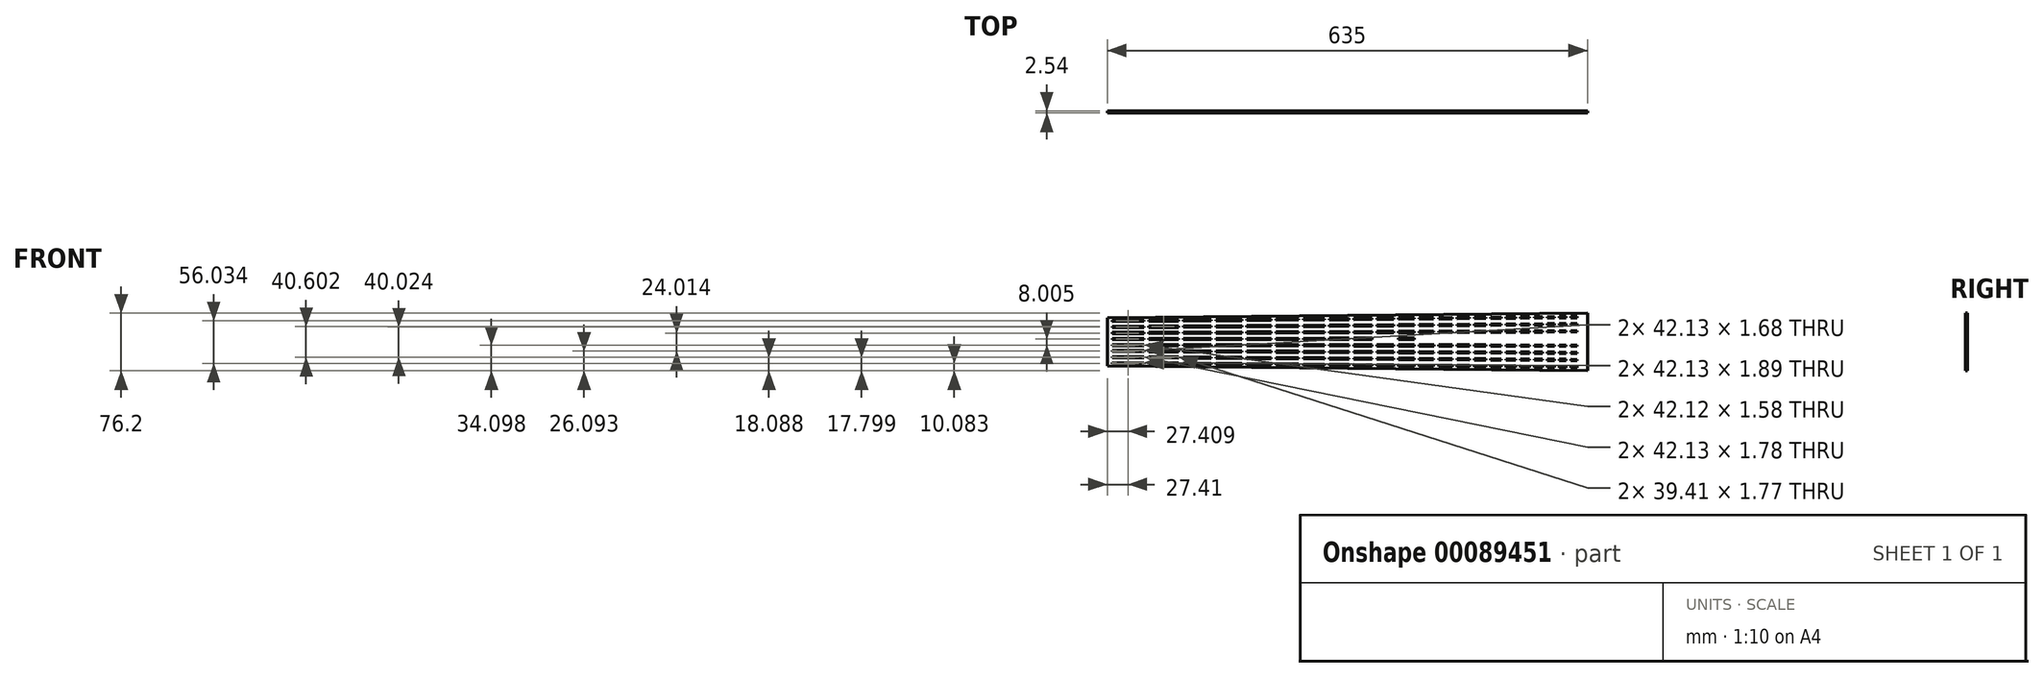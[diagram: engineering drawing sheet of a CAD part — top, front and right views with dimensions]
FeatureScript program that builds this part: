
annotation { "Feature Type Name" : "Feature", "Feature Type Description" : "" }
export const myFeature = defineFeature(function(context is Context, id is Id, definition is map)
    precondition{}
    {
        {
            var Q0;
            Q0=qCreatedBy(makeId("Front.planeOp"),FACE);
            var sketch = newSketch(context, id + "F0", { "sketchPlane" : qUnion([Q0])});
            skLineSegment(sketch, "E0", {"start": v(0, 3.97) * mm, "end": v(646.64, -1.59) * mm, "construction": true});
            skLineSegment(sketch, "E1", {"start": v(0, 4.73) * mm, "end": v(642.96, -0.8) * mm, "construction": true});
            skLineSegment(sketch, "E2", {"start": v(6.35, 3.91) * mm, "end": v(6.36, 4.68) * mm});
            skLineSegment(sketch, "E3", {"start": v(6.36, 4.68) * mm, "end": v(48.48, 4.31) * mm});
            skLineSegment(sketch, "E4", {"start": v(48.48, 4.31) * mm, "end": v(48.47, 3.55) * mm});
            skLineSegment(sketch, "E5", {"start": v(54.82, 3.5) * mm, "end": v(54.82, 4.26) * mm});
            skLineSegment(sketch, "E6", {"start": v(54.82, 4.26) * mm, "end": v(94.22, 3.92) * mm});
            skLineSegment(sketch, "E7", {"start": v(94.22, 3.92) * mm, "end": v(94.22, 3.16) * mm});
            skLineSegment(sketch, "E8", {"start": v(100.57, 3.1) * mm, "end": v(100.57, 3.87) * mm});
            skLineSegment(sketch, "E9", {"start": v(100.57, 3.87) * mm, "end": v(137.4, 3.55) * mm});
            skLineSegment(sketch, "E10", {"start": v(137.4, 3.55) * mm, "end": v(137.4, 2.79) * mm});
            skLineSegment(sketch, "E11", {"start": v(143.75, 2.73) * mm, "end": v(143.75, 3.5) * mm});
            skLineSegment(sketch, "E12", {"start": v(143.75, 3.5) * mm, "end": v(178.15, 3.2) * mm});
            skLineSegment(sketch, "E13", {"start": v(178.15, 3.2) * mm, "end": v(178.15, 2.44) * mm});
            skLineSegment(sketch, "E14", {"start": v(184.5, 2.38) * mm, "end": v(184.5, 3.15) * mm});
            skLineSegment(sketch, "E15", {"start": v(184.5, 3.15) * mm, "end": v(216.63, 2.87) * mm, "construction": true});
            skLineSegment(sketch, "E16", {"start": v(216.63, 2.87) * mm, "end": v(216.62, 2.1) * mm});
            skLineSegment(sketch, "E17", {"start": v(222.97, 2.05) * mm, "end": v(222.98, 2.81) * mm});
            skLineSegment(sketch, "E18", {"start": v(222.98, 2.81) * mm, "end": v(252.94, 2.56) * mm});
            skLineSegment(sketch, "E19", {"start": v(252.94, 2.56) * mm, "end": v(252.93, 1.8) * mm});
            skLineSegment(sketch, "E20", {"start": v(259.28, 1.74) * mm, "end": v(259.29, 2.5) * mm});
            skLineSegment(sketch, "E21", {"start": v(259.29, 2.5) * mm, "end": v(287.21, 2.26) * mm});
            skLineSegment(sketch, "E22", {"start": v(287.21, 2.26) * mm, "end": v(287.2, 1.5) * mm});
            skLineSegment(sketch, "E23", {"start": v(293.56, 1.45) * mm, "end": v(293.56, 2.2) * mm});
            skLineSegment(sketch, "E24", {"start": v(293.56, 2.2) * mm, "end": v(319.56, 1.98) * mm});
            skLineSegment(sketch, "E25", {"start": v(319.56, 1.98) * mm, "end": v(319.55, 1.22) * mm});
            skLineSegment(sketch, "E26", {"start": v(325.9, 1.17) * mm, "end": v(325.91, 1.93) * mm});
            skLineSegment(sketch, "E27", {"start": v(325.91, 1.93) * mm, "end": v(350.1, 1.72) * mm});
            skLineSegment(sketch, "E28", {"start": v(350.1, 1.72) * mm, "end": v(350.09, 0.96) * mm});
            skLineSegment(sketch, "E29", {"start": v(184.5, 3.15) * mm, "end": v(216.63, 2.87) * mm});
            skLineSegment(sketch, "E30", {"start": v(356.44, 0.9) * mm, "end": v(356.44, 1.67) * mm});
            skLineSegment(sketch, "E31", {"start": v(356.44, 1.67) * mm, "end": v(378.91, 1.47) * mm});
            skLineSegment(sketch, "E32", {"start": v(378.91, 1.47) * mm, "end": v(378.9, 0.71) * mm});
            skLineSegment(sketch, "E33", {"start": v(385.26, 0.66) * mm, "end": v(385.26, 1.42) * mm});
            skLineSegment(sketch, "E34", {"start": v(385.26, 1.42) * mm, "end": v(406.12, 1.24) * mm});
            skLineSegment(sketch, "E35", {"start": v(406.12, 1.24) * mm, "end": v(406.1, 0.48) * mm});
            skLineSegment(sketch, "E36", {"start": v(412.46, 0.42) * mm, "end": v(412.46, 1.19) * mm});
            skLineSegment(sketch, "E37", {"start": v(412.46, 1.19) * mm, "end": v(431.8, 1.02) * mm});
            skLineSegment(sketch, "E38", {"start": v(431.8, 1.02) * mm, "end": v(431.78, 0.26) * mm});
            skLineSegment(sketch, "E39", {"start": v(438.13, 0.2) * mm, "end": v(438.14, 0.97) * mm});
            skLineSegment(sketch, "E40", {"start": v(438.14, 0.97) * mm, "end": v(456.02, 0.81) * mm});
            skLineSegment(sketch, "E41", {"start": v(456.02, 0.81) * mm, "end": v(456.02, 0.05) * mm});
            skLineSegment(sketch, "E42", {"start": v(462.37, 0) * mm, "end": v(462.37, 0.76) * mm});
            skLineSegment(sketch, "E43", {"start": v(462.37, 0.76) * mm, "end": v(478.9, 0.62) * mm});
            skLineSegment(sketch, "E44", {"start": v(478.9, 0.62) * mm, "end": v(478.9, -0.15) * mm});
            skLineSegment(sketch, "E45", {"start": v(485.24, -0.2) * mm, "end": v(485.25, 0.56) * mm});
            skLineSegment(sketch, "E46", {"start": v(485.25, 0.56) * mm, "end": v(500.49, 0.43) * mm});
            skLineSegment(sketch, "E47", {"start": v(500.49, 0.43) * mm, "end": v(500.48, -0.33) * mm});
            skLineSegment(sketch, "E48", {"start": v(506.83, -0.39) * mm, "end": v(506.84, 0.38) * mm});
            skLineSegment(sketch, "E49", {"start": v(506.84, 0.38) * mm, "end": v(520.87, 0.26) * mm});
            skLineSegment(sketch, "E50", {"start": v(520.87, 0.26) * mm, "end": v(520.86, -0.5) * mm});
            skLineSegment(sketch, "E51", {"start": v(527.21, -0.56) * mm, "end": v(527.22, 0.2) * mm});
            skLineSegment(sketch, "E52", {"start": v(527.22, 0.2) * mm, "end": v(540.1, 0.09) * mm});
            skLineSegment(sketch, "E53", {"start": v(540.1, 0.09) * mm, "end": v(540.1, -0.67) * mm});
            skLineSegment(sketch, "E54", {"start": v(546.45, -0.73) * mm, "end": v(546.45, 0.04) * mm});
            skLineSegment(sketch, "E55", {"start": v(546.45, 0.04) * mm, "end": v(558.26, -0.07) * mm});
            skLineSegment(sketch, "E56", {"start": v(558.26, -0.07) * mm, "end": v(558.25, -0.83) * mm});
            skLineSegment(sketch, "E57", {"start": v(564.6, -0.88) * mm, "end": v(564.6, -0.12) * mm});
            skLineSegment(sketch, "E58", {"start": v(564.6, -0.12) * mm, "end": v(575.4, -0.21) * mm});
            skLineSegment(sketch, "E59", {"start": v(575.4, -0.21) * mm, "end": v(575.39, -0.98) * mm});
            skLineSegment(sketch, "E60", {"start": v(581.74, -1.03) * mm, "end": v(581.74, -0.27) * mm});
            skLineSegment(sketch, "E61", {"start": v(581.74, -0.27) * mm, "end": v(591.57, -0.35) * mm});
            skLineSegment(sketch, "E62", {"start": v(591.57, -0.35) * mm, "end": v(591.56, -1.11) * mm});
            skLineSegment(sketch, "E63", {"start": v(597.91, -1.17) * mm, "end": v(597.92, -0.4) * mm});
            skLineSegment(sketch, "E64", {"start": v(597.92, -0.4) * mm, "end": v(606.83, -0.48) * mm});
            skLineSegment(sketch, "E65", {"start": v(606.83, -0.48) * mm, "end": v(606.83, -1.25) * mm});
            skLineSegment(sketch, "E66", {"start": v(613.18, -1.3) * mm, "end": v(613.18, -0.54) * mm});
            skLineSegment(sketch, "E67", {"start": v(613.18, -0.54) * mm, "end": v(621.24, -0.6) * mm});
            skLineSegment(sketch, "E68", {"start": v(621.24, -0.6) * mm, "end": v(621.24, -1.37) * mm});
            skLineSegment(sketch, "E69.MirrorCS", {"start": v(184.5, 2.38) * mm, "end": v(184.49, 1.62) * mm});
            skLineSegment(sketch, "E70.MirrorCS", {"start": v(606.82, -2) * mm, "end": v(606.83, -1.25) * mm});
            skLineSegment(sketch, "E71.MirrorCS", {"start": v(222.97, 2.05) * mm, "end": v(222.97, 1.3) * mm});
            skLineSegment(sketch, "E72.MirrorCS", {"start": v(558.24, -1.6) * mm, "end": v(558.25, -0.83) * mm});
            skLineSegment(sketch, "E73.MirrorCS", {"start": v(216.62, 1.35) * mm, "end": v(216.62, 2.1) * mm});
            skLineSegment(sketch, "E74.MirrorCS", {"start": v(293.56, 1.45) * mm, "end": v(293.55, 0.68) * mm});
            skLineSegment(sketch, "E75.MirrorCS", {"start": v(94.2, 2.4) * mm, "end": v(94.22, 3.16) * mm});
            skLineSegment(sketch, "E76.MirrorCS", {"start": v(48.46, 2.8) * mm, "end": v(48.47, 3.55) * mm});
            skLineSegment(sketch, "E77.MirrorCS", {"start": v(613.18, -1.3) * mm, "end": v(613.17, -2.06) * mm});
            skLineSegment(sketch, "E78.MirrorCS", {"start": v(597.91, -1.17) * mm, "end": v(597.9, -1.93) * mm});
            skLineSegment(sketch, "E79.MirrorCS", {"start": v(325.9, 1.17) * mm, "end": v(325.9, 0.4) * mm});
            skLineSegment(sketch, "E80.MirrorCS", {"start": v(581.74, -1.03) * mm, "end": v(581.73, -1.8) * mm});
            skLineSegment(sketch, "E81.MirrorCS", {"start": v(478.89, -0.9) * mm, "end": v(478.9, -0.15) * mm});
            skLineSegment(sketch, "E82.MirrorCS", {"start": v(406.1, -0.28) * mm, "end": v(406.1, 0.48) * mm});
            skLineSegment(sketch, "E83.MirrorCS", {"start": v(591.55, -1.88) * mm, "end": v(591.56, -1.11) * mm});
            skLineSegment(sketch, "E84.MirrorCS", {"start": v(485.24, -0.2) * mm, "end": v(485.24, -0.96) * mm});
            skLineSegment(sketch, "E85.MirrorCS", {"start": v(581.73, -1.8) * mm, "end": v(591.55, -1.88) * mm});
            skLineSegment(sketch, "E86.MirrorCS", {"start": v(520.85, -1.27) * mm, "end": v(520.86, -0.5) * mm});
            skLineSegment(sketch, "E87.MirrorCS", {"start": v(319.55, 0.46) * mm, "end": v(319.55, 1.22) * mm});
            skLineSegment(sketch, "E88.MirrorCS", {"start": v(456.01, -0.71) * mm, "end": v(456.02, 0.05) * mm});
            skLineSegment(sketch, "E89.MirrorCS", {"start": v(564.6, -0.88) * mm, "end": v(564.6, -1.64) * mm});
            skLineSegment(sketch, "E90.MirrorCS", {"start": v(385.26, 0.66) * mm, "end": v(385.25, -0.1) * mm});
            skLineSegment(sketch, "E91.MirrorCS", {"start": v(378.9, -0.05) * mm, "end": v(378.9, 0.71) * mm});
            skLineSegment(sketch, "E92.MirrorCS", {"start": v(506.83, -0.39) * mm, "end": v(506.83, -1.15) * mm});
            skLineSegment(sketch, "E93.MirrorCS", {"start": v(597.9, -1.93) * mm, "end": v(606.82, -2) * mm});
            skLineSegment(sketch, "E94.MirrorCS", {"start": v(546.44, -1.49) * mm, "end": v(558.24, -1.6) * mm});
            skLineSegment(sketch, "E95.MirrorCS", {"start": v(143.75, 2.73) * mm, "end": v(143.74, 1.97) * mm});
            skLineSegment(sketch, "E96.MirrorCS", {"start": v(137.4, 2.03) * mm, "end": v(137.4, 2.79) * mm});
            skLineSegment(sketch, "E97.MirrorCS", {"start": v(100.57, 3.1) * mm, "end": v(100.56, 2.34) * mm});
            skLineSegment(sketch, "E98.MirrorCS", {"start": v(54.82, 3.5) * mm, "end": v(54.81, 2.74) * mm});
            skLineSegment(sketch, "E99.MirrorCS", {"start": v(6.35, 3.91) * mm, "end": v(6.34, 3.15) * mm});
            skLineSegment(sketch, "E100.MirrorCS", {"start": v(178.14, 1.68) * mm, "end": v(178.15, 2.44) * mm});
            skLineSegment(sketch, "E101.MirrorCS", {"start": v(431.78, -0.5) * mm, "end": v(431.78, 0.26) * mm});
            skLineSegment(sketch, "E102.MirrorCS", {"start": v(546.45, -0.73) * mm, "end": v(546.44, -1.49) * mm});
            skLineSegment(sketch, "E103.MirrorCS", {"start": v(500.48, -1.1) * mm, "end": v(500.48, -0.33) * mm});
            skLineSegment(sketch, "E104.MirrorCS", {"start": v(287.2, 0.74) * mm, "end": v(287.2, 1.5) * mm});
            skLineSegment(sketch, "E105.MirrorCS", {"start": v(564.6, -1.64) * mm, "end": v(575.38, -1.74) * mm});
            skLineSegment(sketch, "E106.MirrorCS", {"start": v(252.93, 1.03) * mm, "end": v(252.93, 1.8) * mm});
            skLineSegment(sketch, "E107.MirrorCS", {"start": v(613.17, -2.06) * mm, "end": v(621.23, -2.13) * mm});
            skLineSegment(sketch, "E108.MirrorCS", {"start": v(527.21, -0.56) * mm, "end": v(527.2, -1.32) * mm});
            skLineSegment(sketch, "E109.MirrorCS", {"start": v(350.08, 0.2) * mm, "end": v(350.09, 0.96) * mm});
            skLineSegment(sketch, "E110.MirrorCS", {"start": v(412.46, 0.42) * mm, "end": v(412.45, -0.34) * mm});
            skLineSegment(sketch, "E111.MirrorCS", {"start": v(575.38, -1.74) * mm, "end": v(575.39, -0.98) * mm});
            skLineSegment(sketch, "E112.MirrorCS", {"start": v(259.28, 1.74) * mm, "end": v(259.28, 0.98) * mm});
            skLineSegment(sketch, "E113.MirrorCS", {"start": v(621.23, -2.13) * mm, "end": v(621.24, -1.37) * mm});
            skLineSegment(sketch, "E114.MirrorCS", {"start": v(356.44, 0.9) * mm, "end": v(356.43, 0.14) * mm});
            skLineSegment(sketch, "E115.MirrorCS", {"start": v(506.83, -1.15) * mm, "end": v(520.85, -1.27) * mm});
            skLineSegment(sketch, "E116.MirrorCS", {"start": v(438.13, 0.2) * mm, "end": v(438.13, -0.56) * mm});
            skLineSegment(sketch, "E117.MirrorCS", {"start": v(184.49, 1.62) * mm, "end": v(216.62, 1.35) * mm, "construction": true});
            skLineSegment(sketch, "E118.MirrorCS", {"start": v(462.37, 0) * mm, "end": v(462.36, -0.77) * mm});
            skLineSegment(sketch, "E119.MirrorCS", {"start": v(540.09, -1.43) * mm, "end": v(540.1, -0.67) * mm});
            skLineSegment(sketch, "E120.MirrorCS", {"start": v(527.2, -1.32) * mm, "end": v(540.09, -1.43) * mm});
            skLineSegment(sketch, "E121.MirrorCS", {"start": v(222.97, 1.3) * mm, "end": v(252.93, 1.03) * mm});
            skLineSegment(sketch, "E122.MirrorCS", {"start": v(385.25, -0.1) * mm, "end": v(406.1, -0.28) * mm});
            skLineSegment(sketch, "E123.MirrorCS", {"start": v(293.55, 0.68) * mm, "end": v(319.55, 0.46) * mm});
            skLineSegment(sketch, "E124.MirrorCS", {"start": v(438.13, -0.56) * mm, "end": v(456.01, -0.71) * mm});
            skLineSegment(sketch, "E125.MirrorCS", {"start": v(143.74, 1.97) * mm, "end": v(178.14, 1.68) * mm});
            skLineSegment(sketch, "E126.MirrorCS", {"start": v(54.81, 2.74) * mm, "end": v(94.2, 2.4) * mm});
            skLineSegment(sketch, "E127.MirrorCS", {"start": v(6.34, 3.15) * mm, "end": v(48.46, 2.8) * mm});
            skLineSegment(sketch, "E128.MirrorCS", {"start": v(356.43, 0.14) * mm, "end": v(378.9, -0.05) * mm});
            skLineSegment(sketch, "E129.MirrorCS", {"start": v(259.28, 0.98) * mm, "end": v(287.2, 0.74) * mm});
            skLineSegment(sketch, "E130.MirrorCS", {"start": v(485.24, -0.96) * mm, "end": v(500.48, -1.1) * mm});
            skLineSegment(sketch, "E131.MirrorCS", {"start": v(412.45, -0.34) * mm, "end": v(431.78, -0.5) * mm});
            skLineSegment(sketch, "E132.MirrorCS", {"start": v(184.49, 1.62) * mm, "end": v(216.62, 1.35) * mm});
            skLineSegment(sketch, "E133.MirrorCS", {"start": v(462.36, -0.77) * mm, "end": v(478.89, -0.9) * mm});
            skLineSegment(sketch, "E134.MirrorCS", {"start": v(325.9, 0.4) * mm, "end": v(350.08, 0.2) * mm});
            skLineSegment(sketch, "E135.MirrorCS", {"start": v(100.56, 2.34) * mm, "end": v(137.4, 2.03) * mm});
            skLineSegment(sketch, "E136", {"start": v(-33.04, 0) * mm, "end": v(118.54, 0) * mm, "construction": true});
            skLineSegment(sketch, "E137", {"start": v(0, 11.9) * mm, "end": v(646.65, 7.94) * mm, "construction": true});
            skLineSegment(sketch, "E138", {"start": v(0, 12.67) * mm, "end": v(642.97, 8.72) * mm, "construction": true});
            skLineSegment(sketch, "E139", {"start": v(6.35, 11.87) * mm, "end": v(6.35, 12.63) * mm});
            skLineSegment(sketch, "E140", {"start": v(6.35, 12.63) * mm, "end": v(48.47, 12.37) * mm});
            skLineSegment(sketch, "E141", {"start": v(48.47, 12.37) * mm, "end": v(48.47, 11.6) * mm});
            skLineSegment(sketch, "E142", {"start": v(54.82, 11.57) * mm, "end": v(54.82, 12.33) * mm});
            skLineSegment(sketch, "E143", {"start": v(54.82, 12.33) * mm, "end": v(94.22, 12.09) * mm});
            skLineSegment(sketch, "E144", {"start": v(94.22, 12.09) * mm, "end": v(94.22, 11.33) * mm});
            skLineSegment(sketch, "E145", {"start": v(100.57, 11.29) * mm, "end": v(100.57, 12.05) * mm});
            skLineSegment(sketch, "E146", {"start": v(100.57, 12.05) * mm, "end": v(137.4, 11.82) * mm});
            skLineSegment(sketch, "E147", {"start": v(137.4, 11.82) * mm, "end": v(137.4, 11.06) * mm});
            skLineSegment(sketch, "E148", {"start": v(143.75, 11.02) * mm, "end": v(143.75, 11.79) * mm});
            skLineSegment(sketch, "E149", {"start": v(143.75, 11.79) * mm, "end": v(178.15, 11.57) * mm});
            skLineSegment(sketch, "E150", {"start": v(178.15, 11.57) * mm, "end": v(178.15, 10.81) * mm});
            skLineSegment(sketch, "E151", {"start": v(184.5, 10.77) * mm, "end": v(184.5, 11.54) * mm});
            skLineSegment(sketch, "E152", {"start": v(184.5, 11.54) * mm, "end": v(216.63, 11.34) * mm, "construction": true});
            skLineSegment(sketch, "E153", {"start": v(216.63, 11.34) * mm, "end": v(216.63, 10.58) * mm});
            skLineSegment(sketch, "E154", {"start": v(222.98, 10.54) * mm, "end": v(222.98, 11.3) * mm});
            skLineSegment(sketch, "E155", {"start": v(222.98, 11.3) * mm, "end": v(252.94, 11.12) * mm});
            skLineSegment(sketch, "E156", {"start": v(252.94, 11.12) * mm, "end": v(252.94, 10.35) * mm});
            skLineSegment(sketch, "E157", {"start": v(259.29, 10.31) * mm, "end": v(259.3, 11.08) * mm});
            skLineSegment(sketch, "E158", {"start": v(259.3, 11.08) * mm, "end": v(287.22, 10.9) * mm});
            skLineSegment(sketch, "E159", {"start": v(287.22, 10.9) * mm, "end": v(287.21, 10.14) * mm});
            skLineSegment(sketch, "E160", {"start": v(293.56, 10.1) * mm, "end": v(293.57, 10.87) * mm});
            skLineSegment(sketch, "E161", {"start": v(293.57, 10.87) * mm, "end": v(319.56, 10.7) * mm});
            skLineSegment(sketch, "E162", {"start": v(319.56, 10.7) * mm, "end": v(319.56, 9.94) * mm});
            skLineSegment(sketch, "E163", {"start": v(325.9, 9.9) * mm, "end": v(325.91, 10.67) * mm});
            skLineSegment(sketch, "E164", {"start": v(325.91, 10.67) * mm, "end": v(350.1, 10.52) * mm});
            skLineSegment(sketch, "E165", {"start": v(350.1, 10.52) * mm, "end": v(350.1, 9.76) * mm});
            skLineSegment(sketch, "E166", {"start": v(184.5, 11.54) * mm, "end": v(216.63, 11.34) * mm});
            skLineSegment(sketch, "E167", {"start": v(356.44, 9.72) * mm, "end": v(356.45, 10.48) * mm});
            skLineSegment(sketch, "E168", {"start": v(356.45, 10.48) * mm, "end": v(378.92, 10.34) * mm});
            skLineSegment(sketch, "E169", {"start": v(378.92, 10.34) * mm, "end": v(378.91, 9.58) * mm});
            skLineSegment(sketch, "E170", {"start": v(385.26, 9.54) * mm, "end": v(385.27, 10.3) * mm});
            skLineSegment(sketch, "E171", {"start": v(385.27, 10.3) * mm, "end": v(406.12, 10.18) * mm});
            skLineSegment(sketch, "E172", {"start": v(406.12, 10.18) * mm, "end": v(406.12, 9.41) * mm});
            skLineSegment(sketch, "E173", {"start": v(412.47, 9.37) * mm, "end": v(412.47, 10.14) * mm});
            skLineSegment(sketch, "E174", {"start": v(412.47, 10.14) * mm, "end": v(431.8, 10.02) * mm});
            skLineSegment(sketch, "E175", {"start": v(431.8, 10.02) * mm, "end": v(431.8, 9.26) * mm});
            skLineSegment(sketch, "E176", {"start": v(438.14, 9.22) * mm, "end": v(438.15, 9.98) * mm});
            skLineSegment(sketch, "E177", {"start": v(438.15, 9.98) * mm, "end": v(456.03, 9.87) * mm});
            skLineSegment(sketch, "E178", {"start": v(456.03, 9.87) * mm, "end": v(456.03, 9.1) * mm});
            skLineSegment(sketch, "E179", {"start": v(462.38, 9.07) * mm, "end": v(462.38, 9.83) * mm});
            skLineSegment(sketch, "E180", {"start": v(462.38, 9.83) * mm, "end": v(478.9, 9.73) * mm});
            skLineSegment(sketch, "E181", {"start": v(478.9, 9.73) * mm, "end": v(478.9, 8.97) * mm});
            skLineSegment(sketch, "E182", {"start": v(485.25, 8.93) * mm, "end": v(485.26, 9.7) * mm});
            skLineSegment(sketch, "E183", {"start": v(485.26, 9.7) * mm, "end": v(500.5, 9.6) * mm});
            skLineSegment(sketch, "E184", {"start": v(500.5, 9.6) * mm, "end": v(500.5, 8.83) * mm});
            skLineSegment(sketch, "E185", {"start": v(506.84, 8.8) * mm, "end": v(506.85, 9.56) * mm});
            skLineSegment(sketch, "E186", {"start": v(506.85, 9.56) * mm, "end": v(520.88, 9.47) * mm});
            skLineSegment(sketch, "E187", {"start": v(520.88, 9.47) * mm, "end": v(520.87, 8.7) * mm});
            skLineSegment(sketch, "E188", {"start": v(527.22, 8.67) * mm, "end": v(527.23, 9.43) * mm});
            skLineSegment(sketch, "E189", {"start": v(527.23, 9.43) * mm, "end": v(540.1, 9.35) * mm});
            skLineSegment(sketch, "E190", {"start": v(540.1, 9.35) * mm, "end": v(540.1, 8.6) * mm});
            skLineSegment(sketch, "E191", {"start": v(546.46, 8.55) * mm, "end": v(546.46, 9.31) * mm});
            skLineSegment(sketch, "E192", {"start": v(546.46, 9.31) * mm, "end": v(558.27, 9.24) * mm});
            skLineSegment(sketch, "E193", {"start": v(558.27, 9.24) * mm, "end": v(558.26, 8.48) * mm});
            skLineSegment(sketch, "E194", {"start": v(564.61, 8.44) * mm, "end": v(564.62, 9.2) * mm});
            skLineSegment(sketch, "E195", {"start": v(564.62, 9.2) * mm, "end": v(575.4, 9.14) * mm});
            skLineSegment(sketch, "E196", {"start": v(575.4, 9.14) * mm, "end": v(575.4, 8.37) * mm});
            skLineSegment(sketch, "E197", {"start": v(581.75, 8.34) * mm, "end": v(581.75, 9.1) * mm});
            skLineSegment(sketch, "E198", {"start": v(581.75, 9.1) * mm, "end": v(591.58, 9.04) * mm});
            skLineSegment(sketch, "E199", {"start": v(591.58, 9.04) * mm, "end": v(591.57, 8.28) * mm});
            skLineSegment(sketch, "E200", {"start": v(597.92, 8.24) * mm, "end": v(597.93, 9) * mm});
            skLineSegment(sketch, "E201", {"start": v(597.93, 9) * mm, "end": v(606.84, 8.94) * mm});
            skLineSegment(sketch, "E202", {"start": v(606.84, 8.94) * mm, "end": v(606.84, 8.18) * mm});
            skLineSegment(sketch, "E203", {"start": v(613.19, 8.14) * mm, "end": v(613.2, 8.9) * mm});
            skLineSegment(sketch, "E204", {"start": v(613.2, 8.9) * mm, "end": v(621.25, 8.86) * mm});
            skLineSegment(sketch, "E205", {"start": v(621.25, 8.86) * mm, "end": v(621.25, 8.1) * mm});
            skLineSegment(sketch, "E206.MirrorCS", {"start": v(184.5, 10.77) * mm, "end": v(184.5, 10.01) * mm});
            skLineSegment(sketch, "E207.MirrorCS", {"start": v(606.83, 7.42) * mm, "end": v(606.84, 8.18) * mm});
            skLineSegment(sketch, "E208.MirrorCS", {"start": v(222.98, 10.54) * mm, "end": v(222.97, 9.78) * mm});
            skLineSegment(sketch, "E209.MirrorCS", {"start": v(558.26, 7.72) * mm, "end": v(558.26, 8.48) * mm});
            skLineSegment(sketch, "E210.MirrorCS", {"start": v(216.62, 9.81) * mm, "end": v(216.63, 10.58) * mm});
            skLineSegment(sketch, "E211.MirrorCS", {"start": v(293.56, 10.1) * mm, "end": v(293.56, 9.34) * mm});
            skLineSegment(sketch, "E212.MirrorCS", {"start": v(94.21, 10.57) * mm, "end": v(94.22, 11.33) * mm});
            skLineSegment(sketch, "E213.MirrorCS", {"start": v(48.46, 10.85) * mm, "end": v(48.47, 11.6) * mm});
            skLineSegment(sketch, "E214.MirrorCS", {"start": v(613.19, 8.14) * mm, "end": v(613.18, 7.38) * mm});
            skLineSegment(sketch, "E215.MirrorCS", {"start": v(597.92, 8.24) * mm, "end": v(597.92, 7.47) * mm});
            skLineSegment(sketch, "E216.MirrorCS", {"start": v(325.9, 9.9) * mm, "end": v(325.9, 9.14) * mm});
            skLineSegment(sketch, "E217.MirrorCS", {"start": v(581.75, 8.34) * mm, "end": v(581.74, 7.57) * mm});
            skLineSegment(sketch, "E218.MirrorCS", {"start": v(478.9, 8.2) * mm, "end": v(478.9, 8.97) * mm});
            skLineSegment(sketch, "E219.MirrorCS", {"start": v(406.11, 8.65) * mm, "end": v(406.12, 9.41) * mm});
            skLineSegment(sketch, "E220.MirrorCS", {"start": v(591.57, 7.51) * mm, "end": v(591.57, 8.28) * mm});
            skLineSegment(sketch, "E221.MirrorCS", {"start": v(485.25, 8.93) * mm, "end": v(485.25, 8.17) * mm});
            skLineSegment(sketch, "E222.MirrorCS", {"start": v(581.74, 7.57) * mm, "end": v(591.57, 7.51) * mm});
            skLineSegment(sketch, "E223.MirrorCS", {"start": v(520.87, 7.95) * mm, "end": v(520.87, 8.7) * mm});
            skLineSegment(sketch, "E224.MirrorCS", {"start": v(319.55, 9.18) * mm, "end": v(319.56, 9.94) * mm});
            skLineSegment(sketch, "E225.MirrorCS", {"start": v(456.02, 8.35) * mm, "end": v(456.03, 9.1) * mm});
            skLineSegment(sketch, "E226.MirrorCS", {"start": v(564.61, 8.44) * mm, "end": v(564.6, 7.68) * mm});
            skLineSegment(sketch, "E227.MirrorCS", {"start": v(385.26, 9.54) * mm, "end": v(385.26, 8.78) * mm});
            skLineSegment(sketch, "E228.MirrorCS", {"start": v(378.9, 8.82) * mm, "end": v(378.91, 9.58) * mm});
            skLineSegment(sketch, "E229.MirrorCS", {"start": v(506.84, 8.8) * mm, "end": v(506.84, 8.03) * mm});
            skLineSegment(sketch, "E230.MirrorCS", {"start": v(597.92, 7.47) * mm, "end": v(606.83, 7.42) * mm});
            skLineSegment(sketch, "E231.MirrorCS", {"start": v(546.45, 7.8) * mm, "end": v(558.26, 7.72) * mm});
            skLineSegment(sketch, "E232.MirrorCS", {"start": v(143.75, 11.02) * mm, "end": v(143.74, 10.26) * mm});
            skLineSegment(sketch, "E233.MirrorCS", {"start": v(137.4, 10.3) * mm, "end": v(137.4, 11.06) * mm});
            skLineSegment(sketch, "E234.MirrorCS", {"start": v(100.57, 11.29) * mm, "end": v(100.56, 10.53) * mm});
            skLineSegment(sketch, "E235.MirrorCS", {"start": v(54.82, 11.57) * mm, "end": v(54.81, 10.8) * mm});
            skLineSegment(sketch, "E236.MirrorCS", {"start": v(6.35, 11.87) * mm, "end": v(6.35, 11.1) * mm});
            skLineSegment(sketch, "E237.MirrorCS", {"start": v(178.14, 10.05) * mm, "end": v(178.15, 10.81) * mm});
            skLineSegment(sketch, "E238.MirrorCS", {"start": v(431.79, 8.5) * mm, "end": v(431.8, 9.26) * mm});
            skLineSegment(sketch, "E239.MirrorCS", {"start": v(546.46, 8.55) * mm, "end": v(546.45, 7.8) * mm});
            skLineSegment(sketch, "E240.MirrorCS", {"start": v(500.49, 8.07) * mm, "end": v(500.5, 8.83) * mm});
            skLineSegment(sketch, "E241.MirrorCS", {"start": v(287.2, 9.38) * mm, "end": v(287.21, 10.14) * mm});
            skLineSegment(sketch, "E242.MirrorCS", {"start": v(564.6, 7.68) * mm, "end": v(575.4, 7.61) * mm});
            skLineSegment(sketch, "E243.MirrorCS", {"start": v(252.93, 9.6) * mm, "end": v(252.94, 10.35) * mm});
            skLineSegment(sketch, "E244.MirrorCS", {"start": v(613.18, 7.38) * mm, "end": v(621.24, 7.33) * mm});
            skLineSegment(sketch, "E245.MirrorCS", {"start": v(527.22, 8.67) * mm, "end": v(527.22, 7.9) * mm});
            skLineSegment(sketch, "E246.MirrorCS", {"start": v(350.09, 9) * mm, "end": v(350.1, 9.76) * mm});
            skLineSegment(sketch, "E247.MirrorCS", {"start": v(412.47, 9.37) * mm, "end": v(412.46, 8.61) * mm});
            skLineSegment(sketch, "E248.MirrorCS", {"start": v(575.4, 7.61) * mm, "end": v(575.4, 8.37) * mm});
            skLineSegment(sketch, "E249.MirrorCS", {"start": v(259.29, 10.31) * mm, "end": v(259.28, 9.55) * mm});
            skLineSegment(sketch, "E250.MirrorCS", {"start": v(621.24, 7.33) * mm, "end": v(621.25, 8.1) * mm});
            skLineSegment(sketch, "E251.MirrorCS", {"start": v(356.44, 9.72) * mm, "end": v(356.44, 8.96) * mm});
            skLineSegment(sketch, "E252.MirrorCS", {"start": v(506.84, 8.03) * mm, "end": v(520.87, 7.95) * mm});
            skLineSegment(sketch, "E253.MirrorCS", {"start": v(438.14, 9.22) * mm, "end": v(438.14, 8.46) * mm});
            skLineSegment(sketch, "E254.MirrorCS", {"start": v(184.5, 10.01) * mm, "end": v(216.62, 9.81) * mm, "construction": true});
            skLineSegment(sketch, "E255.MirrorCS", {"start": v(462.38, 9.07) * mm, "end": v(462.37, 8.3) * mm});
            skLineSegment(sketch, "E256.MirrorCS", {"start": v(540.1, 7.83) * mm, "end": v(540.1, 8.6) * mm});
            skLineSegment(sketch, "E257.MirrorCS", {"start": v(527.22, 7.9) * mm, "end": v(540.1, 7.83) * mm});
            skLineSegment(sketch, "E258.MirrorCS", {"start": v(222.97, 9.78) * mm, "end": v(252.93, 9.6) * mm});
            skLineSegment(sketch, "E259.MirrorCS", {"start": v(385.26, 8.78) * mm, "end": v(406.11, 8.65) * mm});
            skLineSegment(sketch, "E260.MirrorCS", {"start": v(293.56, 9.34) * mm, "end": v(319.55, 9.18) * mm});
            skLineSegment(sketch, "E261.MirrorCS", {"start": v(438.14, 8.46) * mm, "end": v(456.02, 8.35) * mm});
            skLineSegment(sketch, "E262.MirrorCS", {"start": v(143.74, 10.26) * mm, "end": v(178.14, 10.05) * mm});
            skLineSegment(sketch, "E263.MirrorCS", {"start": v(54.81, 10.8) * mm, "end": v(94.21, 10.57) * mm});
            skLineSegment(sketch, "E264.MirrorCS", {"start": v(6.35, 11.1) * mm, "end": v(48.46, 10.85) * mm});
            skLineSegment(sketch, "E265.MirrorCS", {"start": v(356.44, 8.96) * mm, "end": v(378.9, 8.82) * mm});
            skLineSegment(sketch, "E266.MirrorCS", {"start": v(259.28, 9.55) * mm, "end": v(287.2, 9.38) * mm});
            skLineSegment(sketch, "E267.MirrorCS", {"start": v(485.25, 8.17) * mm, "end": v(500.49, 8.07) * mm});
            skLineSegment(sketch, "E268.MirrorCS", {"start": v(412.46, 8.61) * mm, "end": v(431.79, 8.5) * mm});
            skLineSegment(sketch, "E269.MirrorCS", {"start": v(184.5, 10.01) * mm, "end": v(216.62, 9.81) * mm});
            skLineSegment(sketch, "E270.MirrorCS", {"start": v(462.37, 8.3) * mm, "end": v(478.9, 8.2) * mm});
            skLineSegment(sketch, "E271.MirrorCS", {"start": v(325.9, 9.14) * mm, "end": v(350.09, 9) * mm});
            skLineSegment(sketch, "E272.MirrorCS", {"start": v(100.56, 10.53) * mm, "end": v(137.4, 10.3) * mm});
            skLineSegment(sketch, "E273", {"start": v(0, 19.84) * mm, "end": v(646.66, 17.46) * mm, "construction": true});
            skLineSegment(sketch, "E274", {"start": v(0, 20.6) * mm, "end": v(642.97, 18.24) * mm, "construction": true});
            skLineSegment(sketch, "E275", {"start": v(6.35, 19.82) * mm, "end": v(6.35, 20.58) * mm});
            skLineSegment(sketch, "E276", {"start": v(6.35, 20.58) * mm, "end": v(48.47, 20.43) * mm});
            skLineSegment(sketch, "E277", {"start": v(48.47, 20.43) * mm, "end": v(48.47, 19.67) * mm});
            skLineSegment(sketch, "E278", {"start": v(54.82, 19.64) * mm, "end": v(54.82, 20.4) * mm});
            skLineSegment(sketch, "E279", {"start": v(54.82, 20.4) * mm, "end": v(94.22, 20.26) * mm});
            skLineSegment(sketch, "E280", {"start": v(94.22, 20.26) * mm, "end": v(94.22, 19.5) * mm});
            skLineSegment(sketch, "E281", {"start": v(100.57, 19.47) * mm, "end": v(100.57, 20.24) * mm});
            skLineSegment(sketch, "E282", {"start": v(100.57, 20.24) * mm, "end": v(137.4, 20.1) * mm});
            skLineSegment(sketch, "E283", {"start": v(137.4, 20.1) * mm, "end": v(137.4, 19.34) * mm});
            skLineSegment(sketch, "E284", {"start": v(143.75, 19.31) * mm, "end": v(143.75, 20.08) * mm});
            skLineSegment(sketch, "E285", {"start": v(143.75, 20.08) * mm, "end": v(178.15, 19.95) * mm});
            skLineSegment(sketch, "E286", {"start": v(178.15, 19.95) * mm, "end": v(178.15, 19.19) * mm});
            skLineSegment(sketch, "E287", {"start": v(184.5, 19.16) * mm, "end": v(184.5, 19.93) * mm});
            skLineSegment(sketch, "E288", {"start": v(184.5, 19.93) * mm, "end": v(216.63, 19.8) * mm, "construction": true});
            skLineSegment(sketch, "E289", {"start": v(216.63, 19.8) * mm, "end": v(216.63, 19.05) * mm});
            skLineSegment(sketch, "E290", {"start": v(222.98, 19.02) * mm, "end": v(222.98, 19.78) * mm});
            skLineSegment(sketch, "E291", {"start": v(222.98, 19.78) * mm, "end": v(252.94, 19.67) * mm});
            skLineSegment(sketch, "E292", {"start": v(252.94, 19.67) * mm, "end": v(252.94, 18.91) * mm});
            skLineSegment(sketch, "E293", {"start": v(259.3, 18.89) * mm, "end": v(259.3, 19.65) * mm});
            skLineSegment(sketch, "E294", {"start": v(259.3, 19.65) * mm, "end": v(287.22, 19.55) * mm});
            skLineSegment(sketch, "E295", {"start": v(287.22, 19.55) * mm, "end": v(287.21, 18.79) * mm});
            skLineSegment(sketch, "E296", {"start": v(293.56, 18.76) * mm, "end": v(293.57, 19.52) * mm});
            skLineSegment(sketch, "E297", {"start": v(293.57, 19.52) * mm, "end": v(319.57, 19.43) * mm});
            skLineSegment(sketch, "E298", {"start": v(319.57, 19.43) * mm, "end": v(319.56, 18.67) * mm});
            skLineSegment(sketch, "E299", {"start": v(325.91, 18.64) * mm, "end": v(325.92, 19.4) * mm});
            skLineSegment(sketch, "E300", {"start": v(325.92, 19.4) * mm, "end": v(350.1, 19.32) * mm});
            skLineSegment(sketch, "E301", {"start": v(350.1, 19.32) * mm, "end": v(350.1, 18.55) * mm});
            skLineSegment(sketch, "E302", {"start": v(184.5, 19.93) * mm, "end": v(216.63, 19.8) * mm});
            skLineSegment(sketch, "E303", {"start": v(356.45, 18.53) * mm, "end": v(356.45, 19.3) * mm});
            skLineSegment(sketch, "E304", {"start": v(356.45, 19.3) * mm, "end": v(378.92, 19.21) * mm});
            skLineSegment(sketch, "E305", {"start": v(378.92, 19.21) * mm, "end": v(378.92, 18.45) * mm});
            skLineSegment(sketch, "E306", {"start": v(385.27, 18.43) * mm, "end": v(385.27, 19.19) * mm});
            skLineSegment(sketch, "E307", {"start": v(385.27, 19.19) * mm, "end": v(406.12, 19.11) * mm});
            skLineSegment(sketch, "E308", {"start": v(406.12, 19.11) * mm, "end": v(406.12, 18.35) * mm});
            skLineSegment(sketch, "E309", {"start": v(412.47, 18.32) * mm, "end": v(412.47, 19.09) * mm});
            skLineSegment(sketch, "E310", {"start": v(412.47, 19.09) * mm, "end": v(431.8, 19.02) * mm});
            skLineSegment(sketch, "E311", {"start": v(431.8, 19.02) * mm, "end": v(431.8, 18.25) * mm});
            skLineSegment(sketch, "E312", {"start": v(438.15, 18.23) * mm, "end": v(438.15, 19) * mm});
            skLineSegment(sketch, "E313", {"start": v(438.15, 19) * mm, "end": v(456.03, 18.93) * mm});
            skLineSegment(sketch, "E314", {"start": v(456.03, 18.93) * mm, "end": v(456.03, 18.16) * mm});
            skLineSegment(sketch, "E315", {"start": v(462.38, 18.14) * mm, "end": v(462.38, 18.9) * mm});
            skLineSegment(sketch, "E316", {"start": v(462.38, 18.9) * mm, "end": v(478.9, 18.84) * mm});
            skLineSegment(sketch, "E317", {"start": v(478.9, 18.84) * mm, "end": v(478.9, 18.08) * mm});
            skLineSegment(sketch, "E318", {"start": v(485.26, 18.06) * mm, "end": v(485.26, 18.82) * mm});
            skLineSegment(sketch, "E319", {"start": v(485.26, 18.82) * mm, "end": v(500.5, 18.76) * mm});
            skLineSegment(sketch, "E320", {"start": v(500.5, 18.76) * mm, "end": v(500.5, 18) * mm});
            skLineSegment(sketch, "E321", {"start": v(506.85, 17.98) * mm, "end": v(506.85, 18.74) * mm});
            skLineSegment(sketch, "E322", {"start": v(506.85, 18.74) * mm, "end": v(520.88, 18.69) * mm});
            skLineSegment(sketch, "E323", {"start": v(520.88, 18.69) * mm, "end": v(520.88, 17.93) * mm});
            skLineSegment(sketch, "E324", {"start": v(527.23, 17.9) * mm, "end": v(527.23, 18.66) * mm});
            skLineSegment(sketch, "E325", {"start": v(527.23, 18.66) * mm, "end": v(540.11, 18.62) * mm});
            skLineSegment(sketch, "E326", {"start": v(540.11, 18.62) * mm, "end": v(540.11, 17.85) * mm});
            skLineSegment(sketch, "E327", {"start": v(546.46, 17.83) * mm, "end": v(546.46, 18.6) * mm});
            skLineSegment(sketch, "E328", {"start": v(546.46, 18.6) * mm, "end": v(558.27, 18.55) * mm});
            skLineSegment(sketch, "E329", {"start": v(558.27, 18.55) * mm, "end": v(558.27, 17.79) * mm});
            skLineSegment(sketch, "E330", {"start": v(564.62, 17.76) * mm, "end": v(564.62, 18.53) * mm});
            skLineSegment(sketch, "E331", {"start": v(564.62, 18.53) * mm, "end": v(575.4, 18.49) * mm});
            skLineSegment(sketch, "E332", {"start": v(575.4, 18.49) * mm, "end": v(575.4, 17.72) * mm});
            skLineSegment(sketch, "E333", {"start": v(581.75, 17.7) * mm, "end": v(581.76, 18.46) * mm});
            skLineSegment(sketch, "E334", {"start": v(581.76, 18.46) * mm, "end": v(591.58, 18.43) * mm});
            skLineSegment(sketch, "E335", {"start": v(591.58, 18.43) * mm, "end": v(591.58, 17.67) * mm});
            skLineSegment(sketch, "E336", {"start": v(597.93, 17.64) * mm, "end": v(597.93, 18.4) * mm});
            skLineSegment(sketch, "E337", {"start": v(597.93, 18.4) * mm, "end": v(606.85, 18.37) * mm});
            skLineSegment(sketch, "E338", {"start": v(606.85, 18.37) * mm, "end": v(606.85, 17.6) * mm});
            skLineSegment(sketch, "E339", {"start": v(613.2, 17.59) * mm, "end": v(613.2, 18.35) * mm});
            skLineSegment(sketch, "E340", {"start": v(613.2, 18.35) * mm, "end": v(621.26, 18.32) * mm});
            skLineSegment(sketch, "E341", {"start": v(621.26, 18.32) * mm, "end": v(621.26, 17.56) * mm});
            skLineSegment(sketch, "E342.MirrorCS", {"start": v(184.5, 19.16) * mm, "end": v(184.5, 18.4) * mm});
            skLineSegment(sketch, "E343.MirrorCS", {"start": v(606.84, 16.85) * mm, "end": v(606.85, 17.6) * mm});
            skLineSegment(sketch, "E344.MirrorCS", {"start": v(222.98, 19.02) * mm, "end": v(222.98, 18.26) * mm});
            skLineSegment(sketch, "E345.MirrorCS", {"start": v(558.27, 17.03) * mm, "end": v(558.27, 17.79) * mm});
            skLineSegment(sketch, "E346.MirrorCS", {"start": v(216.63, 18.28) * mm, "end": v(216.63, 19.05) * mm});
            skLineSegment(sketch, "E347.MirrorCS", {"start": v(293.56, 18.76) * mm, "end": v(293.56, 18) * mm});
            skLineSegment(sketch, "E348.MirrorCS", {"start": v(94.22, 18.73) * mm, "end": v(94.22, 19.5) * mm});
            skLineSegment(sketch, "E349.MirrorCS", {"start": v(48.47, 18.9) * mm, "end": v(48.47, 19.67) * mm});
            skLineSegment(sketch, "E350.MirrorCS", {"start": v(613.2, 17.59) * mm, "end": v(613.2, 16.82) * mm});
            skLineSegment(sketch, "E351.MirrorCS", {"start": v(597.93, 17.64) * mm, "end": v(597.93, 16.88) * mm});
            skLineSegment(sketch, "E352.MirrorCS", {"start": v(325.91, 18.64) * mm, "end": v(325.91, 17.88) * mm});
            skLineSegment(sketch, "E353.MirrorCS", {"start": v(581.75, 17.7) * mm, "end": v(581.75, 16.94) * mm});
            skLineSegment(sketch, "E354.MirrorCS", {"start": v(478.9, 17.32) * mm, "end": v(478.9, 18.08) * mm});
            skLineSegment(sketch, "E355.MirrorCS", {"start": v(406.12, 17.59) * mm, "end": v(406.12, 18.35) * mm});
            skLineSegment(sketch, "E356.MirrorCS", {"start": v(591.58, 16.9) * mm, "end": v(591.58, 17.67) * mm});
            skLineSegment(sketch, "E357.MirrorCS", {"start": v(485.26, 18.06) * mm, "end": v(485.25, 17.3) * mm});
            skLineSegment(sketch, "E358.MirrorCS", {"start": v(581.75, 16.94) * mm, "end": v(591.58, 16.9) * mm});
            skLineSegment(sketch, "E359.MirrorCS", {"start": v(520.87, 17.16) * mm, "end": v(520.88, 17.93) * mm});
            skLineSegment(sketch, "E360.MirrorCS", {"start": v(319.56, 17.9) * mm, "end": v(319.56, 18.67) * mm});
            skLineSegment(sketch, "E361.MirrorCS", {"start": v(456.03, 17.4) * mm, "end": v(456.03, 18.16) * mm});
            skLineSegment(sketch, "E362.MirrorCS", {"start": v(564.62, 17.76) * mm, "end": v(564.61, 17) * mm});
            skLineSegment(sketch, "E363.MirrorCS", {"start": v(385.27, 18.43) * mm, "end": v(385.27, 17.66) * mm});
            skLineSegment(sketch, "E364.MirrorCS", {"start": v(378.92, 17.69) * mm, "end": v(378.92, 18.45) * mm});
            skLineSegment(sketch, "E365.MirrorCS", {"start": v(506.85, 17.98) * mm, "end": v(506.84, 17.22) * mm});
            skLineSegment(sketch, "E366.MirrorCS", {"start": v(597.93, 16.88) * mm, "end": v(606.84, 16.85) * mm});
            skLineSegment(sketch, "E367.MirrorCS", {"start": v(546.46, 17.07) * mm, "end": v(558.27, 17.03) * mm});
            skLineSegment(sketch, "E368.MirrorCS", {"start": v(143.75, 19.31) * mm, "end": v(143.75, 18.55) * mm});
            skLineSegment(sketch, "E369.MirrorCS", {"start": v(137.4, 18.58) * mm, "end": v(137.4, 19.34) * mm});
            skLineSegment(sketch, "E370.MirrorCS", {"start": v(100.57, 19.47) * mm, "end": v(100.57, 18.71) * mm});
            skLineSegment(sketch, "E371.MirrorCS", {"start": v(54.82, 19.64) * mm, "end": v(54.82, 18.88) * mm});
            skLineSegment(sketch, "E372.MirrorCS", {"start": v(6.35, 19.82) * mm, "end": v(6.35, 19.06) * mm});
            skLineSegment(sketch, "E373.MirrorCS", {"start": v(178.15, 18.43) * mm, "end": v(178.15, 19.19) * mm});
            skLineSegment(sketch, "E374.MirrorCS", {"start": v(431.8, 17.5) * mm, "end": v(431.8, 18.25) * mm});
            skLineSegment(sketch, "E375.MirrorCS", {"start": v(546.46, 17.83) * mm, "end": v(546.46, 17.07) * mm});
            skLineSegment(sketch, "E376.MirrorCS", {"start": v(500.5, 17.24) * mm, "end": v(500.5, 18) * mm});
            skLineSegment(sketch, "E377.MirrorCS", {"start": v(287.21, 18.02) * mm, "end": v(287.21, 18.79) * mm});
            skLineSegment(sketch, "E378.MirrorCS", {"start": v(564.61, 17) * mm, "end": v(575.4, 16.96) * mm});
            skLineSegment(sketch, "E379.MirrorCS", {"start": v(252.94, 18.15) * mm, "end": v(252.94, 18.91) * mm});
            skLineSegment(sketch, "E380.MirrorCS", {"start": v(613.2, 16.82) * mm, "end": v(621.25, 16.8) * mm});
            skLineSegment(sketch, "E381.MirrorCS", {"start": v(527.23, 17.9) * mm, "end": v(527.22, 17.14) * mm});
            skLineSegment(sketch, "E382.MirrorCS", {"start": v(350.1, 17.8) * mm, "end": v(350.1, 18.55) * mm});
            skLineSegment(sketch, "E383.MirrorCS", {"start": v(412.47, 18.32) * mm, "end": v(412.47, 17.56) * mm});
            skLineSegment(sketch, "E384.MirrorCS", {"start": v(575.4, 16.96) * mm, "end": v(575.4, 17.72) * mm});
            skLineSegment(sketch, "E385.MirrorCS", {"start": v(259.3, 18.89) * mm, "end": v(259.29, 18.13) * mm});
            skLineSegment(sketch, "E386.MirrorCS", {"start": v(621.25, 16.8) * mm, "end": v(621.26, 17.56) * mm});
            skLineSegment(sketch, "E387.MirrorCS", {"start": v(356.45, 18.53) * mm, "end": v(356.44, 17.77) * mm});
            skLineSegment(sketch, "E388.MirrorCS", {"start": v(506.84, 17.22) * mm, "end": v(520.87, 17.16) * mm});
            skLineSegment(sketch, "E389.MirrorCS", {"start": v(438.15, 18.23) * mm, "end": v(438.14, 17.47) * mm});
            skLineSegment(sketch, "E390.MirrorCS", {"start": v(184.5, 18.4) * mm, "end": v(216.63, 18.28) * mm, "construction": true});
            skLineSegment(sketch, "E391.MirrorCS", {"start": v(462.38, 18.14) * mm, "end": v(462.38, 17.38) * mm});
            skLineSegment(sketch, "E392.MirrorCS", {"start": v(540.1, 17.1) * mm, "end": v(540.11, 17.85) * mm});
            skLineSegment(sketch, "E393.MirrorCS", {"start": v(527.22, 17.14) * mm, "end": v(540.1, 17.1) * mm});
            skLineSegment(sketch, "E394.MirrorCS", {"start": v(222.98, 18.26) * mm, "end": v(252.94, 18.15) * mm});
            skLineSegment(sketch, "E395.MirrorCS", {"start": v(385.27, 17.66) * mm, "end": v(406.12, 17.59) * mm});
            skLineSegment(sketch, "E396.MirrorCS", {"start": v(293.56, 18) * mm, "end": v(319.56, 17.9) * mm});
            skLineSegment(sketch, "E397.MirrorCS", {"start": v(438.14, 17.47) * mm, "end": v(456.03, 17.4) * mm});
            skLineSegment(sketch, "E398.MirrorCS", {"start": v(143.75, 18.55) * mm, "end": v(178.15, 18.43) * mm});
            skLineSegment(sketch, "E399.MirrorCS", {"start": v(54.82, 18.88) * mm, "end": v(94.22, 18.73) * mm});
            skLineSegment(sketch, "E400.MirrorCS", {"start": v(6.35, 19.06) * mm, "end": v(48.47, 18.9) * mm});
            skLineSegment(sketch, "E401.MirrorCS", {"start": v(356.44, 17.77) * mm, "end": v(378.92, 17.69) * mm});
            skLineSegment(sketch, "E402.MirrorCS", {"start": v(259.29, 18.13) * mm, "end": v(287.21, 18.02) * mm});
            skLineSegment(sketch, "E403.MirrorCS", {"start": v(485.25, 17.3) * mm, "end": v(500.5, 17.24) * mm});
            skLineSegment(sketch, "E404.MirrorCS", {"start": v(412.47, 17.56) * mm, "end": v(431.8, 17.5) * mm});
            skLineSegment(sketch, "E405.MirrorCS", {"start": v(184.5, 18.4) * mm, "end": v(216.63, 18.28) * mm});
            skLineSegment(sketch, "E406.MirrorCS", {"start": v(462.38, 17.38) * mm, "end": v(478.9, 17.32) * mm});
            skLineSegment(sketch, "E407.MirrorCS", {"start": v(325.91, 17.88) * mm, "end": v(350.1, 17.8) * mm});
            skLineSegment(sketch, "E408.MirrorCS", {"start": v(100.57, 18.71) * mm, "end": v(137.4, 18.58) * mm});
            skLineSegment(sketch, "E409", {"start": v(0, 27.78) * mm, "end": v(646.66, 26.99) * mm, "construction": true});
            skLineSegment(sketch, "E410", {"start": v(0, 28.54) * mm, "end": v(642.98, 27.75) * mm, "construction": true});
            skLineSegment(sketch, "E411", {"start": v(6.35, 27.77) * mm, "end": v(6.35, 28.54) * mm});
            skLineSegment(sketch, "E412", {"start": v(6.35, 28.54) * mm, "end": v(48.47, 28.48) * mm});
            skLineSegment(sketch, "E413", {"start": v(48.47, 28.48) * mm, "end": v(48.47, 27.72) * mm});
            skLineSegment(sketch, "E414", {"start": v(54.82, 27.71) * mm, "end": v(54.82, 28.48) * mm});
            skLineSegment(sketch, "E415", {"start": v(54.82, 28.48) * mm, "end": v(94.22, 28.43) * mm});
            skLineSegment(sketch, "E416", {"start": v(94.22, 28.43) * mm, "end": v(94.22, 27.67) * mm});
            skLineSegment(sketch, "E417", {"start": v(100.57, 27.66) * mm, "end": v(100.57, 28.42) * mm});
            skLineSegment(sketch, "E418", {"start": v(100.57, 28.42) * mm, "end": v(137.4, 28.37) * mm});
            skLineSegment(sketch, "E419", {"start": v(137.4, 28.37) * mm, "end": v(137.4, 27.61) * mm});
            skLineSegment(sketch, "E420", {"start": v(143.75, 27.6) * mm, "end": v(143.75, 28.37) * mm});
            skLineSegment(sketch, "E421", {"start": v(143.75, 28.37) * mm, "end": v(178.15, 28.32) * mm});
            skLineSegment(sketch, "E422", {"start": v(178.15, 28.32) * mm, "end": v(178.15, 27.56) * mm});
            skLineSegment(sketch, "E423", {"start": v(184.5, 27.55) * mm, "end": v(184.5, 28.32) * mm});
            skLineSegment(sketch, "E424", {"start": v(184.5, 28.32) * mm, "end": v(216.63, 28.28) * mm, "construction": true});
            skLineSegment(sketch, "E425", {"start": v(216.63, 28.28) * mm, "end": v(216.63, 27.52) * mm});
            skLineSegment(sketch, "E426", {"start": v(222.98, 27.5) * mm, "end": v(222.98, 28.27) * mm});
            skLineSegment(sketch, "E427", {"start": v(222.98, 28.27) * mm, "end": v(252.94, 28.23) * mm});
            skLineSegment(sketch, "E428", {"start": v(252.94, 28.23) * mm, "end": v(252.94, 27.47) * mm});
            skLineSegment(sketch, "E429", {"start": v(259.3, 27.46) * mm, "end": v(259.3, 28.22) * mm});
            skLineSegment(sketch, "E430", {"start": v(259.3, 28.22) * mm, "end": v(287.22, 28.2) * mm});
            skLineSegment(sketch, "E431", {"start": v(287.22, 28.2) * mm, "end": v(287.22, 27.43) * mm});
            skLineSegment(sketch, "E432", {"start": v(293.57, 27.42) * mm, "end": v(293.57, 28.18) * mm});
            skLineSegment(sketch, "E433", {"start": v(293.57, 28.18) * mm, "end": v(319.57, 28.15) * mm});
            skLineSegment(sketch, "E434", {"start": v(319.57, 28.15) * mm, "end": v(319.57, 27.39) * mm});
            skLineSegment(sketch, "E435", {"start": v(325.92, 27.38) * mm, "end": v(325.92, 28.14) * mm});
            skLineSegment(sketch, "E436", {"start": v(325.92, 28.14) * mm, "end": v(350.1, 28.11) * mm});
            skLineSegment(sketch, "E437", {"start": v(350.1, 28.11) * mm, "end": v(350.1, 27.35) * mm});
            skLineSegment(sketch, "E438", {"start": v(184.5, 28.32) * mm, "end": v(216.63, 28.28) * mm});
            skLineSegment(sketch, "E439", {"start": v(356.45, 27.34) * mm, "end": v(356.45, 28.1) * mm});
            skLineSegment(sketch, "E440", {"start": v(356.45, 28.1) * mm, "end": v(378.92, 28.08) * mm});
            skLineSegment(sketch, "E441", {"start": v(378.92, 28.08) * mm, "end": v(378.92, 27.32) * mm});
            skLineSegment(sketch, "E442", {"start": v(385.27, 27.3) * mm, "end": v(385.27, 28.07) * mm});
            skLineSegment(sketch, "E443", {"start": v(385.27, 28.07) * mm, "end": v(406.12, 28.04) * mm});
            skLineSegment(sketch, "E444", {"start": v(406.12, 28.04) * mm, "end": v(406.12, 27.28) * mm});
            skLineSegment(sketch, "E445", {"start": v(412.47, 27.27) * mm, "end": v(412.47, 28.04) * mm});
            skLineSegment(sketch, "E446", {"start": v(412.47, 28.04) * mm, "end": v(431.8, 28.01) * mm});
            skLineSegment(sketch, "E447", {"start": v(431.8, 28.01) * mm, "end": v(431.8, 27.25) * mm});
            skLineSegment(sketch, "E448", {"start": v(438.15, 27.24) * mm, "end": v(438.15, 28) * mm});
            skLineSegment(sketch, "E449", {"start": v(438.15, 28) * mm, "end": v(456.04, 27.98) * mm});
            skLineSegment(sketch, "E450", {"start": v(456.04, 27.98) * mm, "end": v(456.03, 27.22) * mm});
            skLineSegment(sketch, "E451", {"start": v(462.38, 27.21) * mm, "end": v(462.39, 27.98) * mm});
            skLineSegment(sketch, "E452", {"start": v(462.39, 27.98) * mm, "end": v(478.91, 27.96) * mm});
            skLineSegment(sketch, "E453", {"start": v(478.91, 27.96) * mm, "end": v(478.9, 27.2) * mm});
            skLineSegment(sketch, "E454", {"start": v(485.26, 27.19) * mm, "end": v(485.26, 27.95) * mm});
            skLineSegment(sketch, "E455", {"start": v(485.26, 27.95) * mm, "end": v(500.5, 27.93) * mm});
            skLineSegment(sketch, "E456", {"start": v(500.5, 27.93) * mm, "end": v(500.5, 27.17) * mm});
            skLineSegment(sketch, "E457", {"start": v(506.85, 27.16) * mm, "end": v(506.85, 27.92) * mm});
            skLineSegment(sketch, "E458", {"start": v(506.85, 27.92) * mm, "end": v(520.88, 27.9) * mm});
            skLineSegment(sketch, "E459", {"start": v(520.88, 27.9) * mm, "end": v(520.88, 27.14) * mm});
            skLineSegment(sketch, "E460", {"start": v(527.23, 27.13) * mm, "end": v(527.23, 27.9) * mm});
            skLineSegment(sketch, "E461", {"start": v(527.23, 27.9) * mm, "end": v(540.12, 27.88) * mm});
            skLineSegment(sketch, "E462", {"start": v(540.12, 27.88) * mm, "end": v(540.11, 27.12) * mm});
            skLineSegment(sketch, "E463", {"start": v(546.46, 27.11) * mm, "end": v(546.47, 27.87) * mm});
            skLineSegment(sketch, "E464", {"start": v(546.47, 27.87) * mm, "end": v(558.27, 27.86) * mm});
            skLineSegment(sketch, "E465", {"start": v(558.27, 27.86) * mm, "end": v(558.27, 27.1) * mm});
            skLineSegment(sketch, "E466", {"start": v(564.62, 27.09) * mm, "end": v(564.62, 27.85) * mm});
            skLineSegment(sketch, "E467", {"start": v(564.62, 27.85) * mm, "end": v(575.4, 27.84) * mm});
            skLineSegment(sketch, "E468", {"start": v(575.4, 27.84) * mm, "end": v(575.4, 27.07) * mm});
            skLineSegment(sketch, "E469", {"start": v(581.76, 27.07) * mm, "end": v(581.76, 27.83) * mm});
            skLineSegment(sketch, "E470", {"start": v(581.76, 27.83) * mm, "end": v(591.58, 27.82) * mm});
            skLineSegment(sketch, "E471", {"start": v(591.58, 27.82) * mm, "end": v(591.58, 27.06) * mm});
            skLineSegment(sketch, "E472", {"start": v(597.93, 27.05) * mm, "end": v(597.93, 27.8) * mm});
            skLineSegment(sketch, "E473", {"start": v(597.93, 27.8) * mm, "end": v(606.85, 27.8) * mm});
            skLineSegment(sketch, "E474", {"start": v(606.85, 27.8) * mm, "end": v(606.85, 27.04) * mm});
            skLineSegment(sketch, "E475", {"start": v(613.2, 27.03) * mm, "end": v(613.2, 27.8) * mm});
            skLineSegment(sketch, "E476", {"start": v(613.2, 27.8) * mm, "end": v(621.26, 27.78) * mm});
            skLineSegment(sketch, "E477", {"start": v(621.26, 27.78) * mm, "end": v(621.26, 27.02) * mm});
            skLineSegment(sketch, "E478.MirrorCS", {"start": v(184.5, 27.55) * mm, "end": v(184.5, 26.8) * mm});
            skLineSegment(sketch, "E479.MirrorCS", {"start": v(606.85, 26.27) * mm, "end": v(606.85, 27.04) * mm});
            skLineSegment(sketch, "E480.MirrorCS", {"start": v(222.98, 27.5) * mm, "end": v(222.98, 26.75) * mm});
            skLineSegment(sketch, "E481.MirrorCS", {"start": v(558.27, 26.33) * mm, "end": v(558.27, 27.1) * mm});
            skLineSegment(sketch, "E482.MirrorCS", {"start": v(216.63, 26.75) * mm, "end": v(216.63, 27.52) * mm});
            skLineSegment(sketch, "E483.MirrorCS", {"start": v(293.57, 27.42) * mm, "end": v(293.56, 26.66) * mm});
            skLineSegment(sketch, "E484.MirrorCS", {"start": v(94.22, 26.9) * mm, "end": v(94.22, 27.67) * mm});
            skLineSegment(sketch, "E485.MirrorCS", {"start": v(48.47, 26.96) * mm, "end": v(48.47, 27.72) * mm});
            skLineSegment(sketch, "E486.MirrorCS", {"start": v(613.2, 27.03) * mm, "end": v(613.2, 26.27) * mm});
            skLineSegment(sketch, "E487.MirrorCS", {"start": v(597.93, 27.05) * mm, "end": v(597.93, 26.29) * mm});
            skLineSegment(sketch, "E488.MirrorCS", {"start": v(325.92, 27.38) * mm, "end": v(325.91, 26.62) * mm});
            skLineSegment(sketch, "E489.MirrorCS", {"start": v(581.76, 27.07) * mm, "end": v(581.76, 26.3) * mm});
            skLineSegment(sketch, "E490.MirrorCS", {"start": v(478.9, 26.43) * mm, "end": v(478.9, 27.2) * mm});
            skLineSegment(sketch, "E491.MirrorCS", {"start": v(406.12, 26.52) * mm, "end": v(406.12, 27.28) * mm});
            skLineSegment(sketch, "E492.MirrorCS", {"start": v(591.58, 26.3) * mm, "end": v(591.58, 27.06) * mm});
            skLineSegment(sketch, "E493.MirrorCS", {"start": v(485.26, 27.19) * mm, "end": v(485.26, 26.42) * mm});
            skLineSegment(sketch, "E494.MirrorCS", {"start": v(581.76, 26.3) * mm, "end": v(591.58, 26.3) * mm});
            skLineSegment(sketch, "E495.MirrorCS", {"start": v(520.88, 26.38) * mm, "end": v(520.88, 27.14) * mm});
            skLineSegment(sketch, "E496.MirrorCS", {"start": v(319.56, 26.63) * mm, "end": v(319.57, 27.39) * mm});
            skLineSegment(sketch, "E497.MirrorCS", {"start": v(456.03, 26.46) * mm, "end": v(456.03, 27.22) * mm});
            skLineSegment(sketch, "E498.MirrorCS", {"start": v(564.62, 27.09) * mm, "end": v(564.62, 26.33) * mm});
            skLineSegment(sketch, "E499.MirrorCS", {"start": v(385.27, 27.3) * mm, "end": v(385.27, 26.55) * mm});
            skLineSegment(sketch, "E500.MirrorCS", {"start": v(378.92, 26.55) * mm, "end": v(378.92, 27.32) * mm});
            skLineSegment(sketch, "E501.MirrorCS", {"start": v(506.85, 27.16) * mm, "end": v(506.85, 26.4) * mm});
            skLineSegment(sketch, "E502.MirrorCS", {"start": v(597.93, 26.29) * mm, "end": v(606.85, 26.27) * mm});
            skLineSegment(sketch, "E503.MirrorCS", {"start": v(546.46, 26.35) * mm, "end": v(558.27, 26.33) * mm});
            skLineSegment(sketch, "E504.MirrorCS", {"start": v(143.75, 27.6) * mm, "end": v(143.75, 26.84) * mm});
            skLineSegment(sketch, "E505.MirrorCS", {"start": v(137.4, 26.85) * mm, "end": v(137.4, 27.61) * mm});
            skLineSegment(sketch, "E506.MirrorCS", {"start": v(100.57, 27.66) * mm, "end": v(100.57, 26.9) * mm});
            skLineSegment(sketch, "E507.MirrorCS", {"start": v(54.82, 27.71) * mm, "end": v(54.82, 26.95) * mm});
            skLineSegment(sketch, "E508.MirrorCS", {"start": v(6.35, 27.77) * mm, "end": v(6.35, 27.01) * mm});
            skLineSegment(sketch, "E509.MirrorCS", {"start": v(178.15, 26.8) * mm, "end": v(178.15, 27.56) * mm});
            skLineSegment(sketch, "E510.MirrorCS", {"start": v(431.8, 26.49) * mm, "end": v(431.8, 27.25) * mm});
            skLineSegment(sketch, "E511.MirrorCS", {"start": v(546.46, 27.11) * mm, "end": v(546.46, 26.35) * mm});
            skLineSegment(sketch, "E512.MirrorCS", {"start": v(500.5, 26.4) * mm, "end": v(500.5, 27.17) * mm});
            skLineSegment(sketch, "E513.MirrorCS", {"start": v(287.21, 26.67) * mm, "end": v(287.22, 27.43) * mm});
            skLineSegment(sketch, "E514.MirrorCS", {"start": v(564.62, 26.33) * mm, "end": v(575.4, 26.31) * mm});
            skLineSegment(sketch, "E515.MirrorCS", {"start": v(252.94, 26.7) * mm, "end": v(252.94, 27.47) * mm});
            skLineSegment(sketch, "E516.MirrorCS", {"start": v(613.2, 26.27) * mm, "end": v(621.26, 26.26) * mm});
            skLineSegment(sketch, "E517.MirrorCS", {"start": v(527.23, 27.13) * mm, "end": v(527.23, 26.37) * mm});
            skLineSegment(sketch, "E518.MirrorCS", {"start": v(350.1, 26.59) * mm, "end": v(350.1, 27.35) * mm});
            skLineSegment(sketch, "E519.MirrorCS", {"start": v(412.47, 27.27) * mm, "end": v(412.47, 26.51) * mm});
            skLineSegment(sketch, "E520.MirrorCS", {"start": v(575.4, 26.31) * mm, "end": v(575.4, 27.07) * mm});
            skLineSegment(sketch, "E521.MirrorCS", {"start": v(259.3, 27.46) * mm, "end": v(259.3, 26.7) * mm});
            skLineSegment(sketch, "E522.MirrorCS", {"start": v(621.26, 26.26) * mm, "end": v(621.26, 27.02) * mm});
            skLineSegment(sketch, "E523.MirrorCS", {"start": v(356.45, 27.34) * mm, "end": v(356.45, 26.58) * mm});
            skLineSegment(sketch, "E524.MirrorCS", {"start": v(506.85, 26.4) * mm, "end": v(520.88, 26.38) * mm});
            skLineSegment(sketch, "E525.MirrorCS", {"start": v(438.15, 27.24) * mm, "end": v(438.15, 26.48) * mm});
            skLineSegment(sketch, "E526.MirrorCS", {"start": v(184.5, 26.8) * mm, "end": v(216.63, 26.75) * mm, "construction": true});
            skLineSegment(sketch, "E527.MirrorCS", {"start": v(462.38, 27.21) * mm, "end": v(462.38, 26.45) * mm});
            skLineSegment(sketch, "E528.MirrorCS", {"start": v(540.11, 26.36) * mm, "end": v(540.11, 27.12) * mm});
            skLineSegment(sketch, "E529.MirrorCS", {"start": v(527.23, 26.37) * mm, "end": v(540.11, 26.36) * mm});
            skLineSegment(sketch, "E530.MirrorCS", {"start": v(222.98, 26.75) * mm, "end": v(252.94, 26.7) * mm});
            skLineSegment(sketch, "E531.MirrorCS", {"start": v(385.27, 26.55) * mm, "end": v(406.12, 26.52) * mm});
            skLineSegment(sketch, "E532.MirrorCS", {"start": v(293.56, 26.66) * mm, "end": v(319.56, 26.63) * mm});
            skLineSegment(sketch, "E533.MirrorCS", {"start": v(438.15, 26.48) * mm, "end": v(456.03, 26.46) * mm});
            skLineSegment(sketch, "E534.MirrorCS", {"start": v(143.75, 26.84) * mm, "end": v(178.15, 26.8) * mm});
            skLineSegment(sketch, "E535.MirrorCS", {"start": v(54.82, 26.95) * mm, "end": v(94.22, 26.9) * mm});
            skLineSegment(sketch, "E536.MirrorCS", {"start": v(6.35, 27.01) * mm, "end": v(48.47, 26.96) * mm});
            skLineSegment(sketch, "E537.MirrorCS", {"start": v(356.45, 26.58) * mm, "end": v(378.92, 26.55) * mm});
            skLineSegment(sketch, "E538.MirrorCS", {"start": v(259.3, 26.7) * mm, "end": v(287.21, 26.67) * mm});
            skLineSegment(sketch, "E539.MirrorCS", {"start": v(485.26, 26.42) * mm, "end": v(500.5, 26.4) * mm});
            skLineSegment(sketch, "E540.MirrorCS", {"start": v(412.47, 26.51) * mm, "end": v(431.8, 26.49) * mm});
            skLineSegment(sketch, "E541.MirrorCS", {"start": v(184.5, 26.8) * mm, "end": v(216.63, 26.75) * mm});
            skLineSegment(sketch, "E542.MirrorCS", {"start": v(462.38, 26.45) * mm, "end": v(478.9, 26.43) * mm});
            skLineSegment(sketch, "E543.MirrorCS", {"start": v(325.91, 26.62) * mm, "end": v(350.1, 26.59) * mm});
            skLineSegment(sketch, "E544.MirrorCS", {"start": v(100.57, 26.9) * mm, "end": v(137.4, 26.85) * mm});
            skLineSegment(sketch, "E545", {"start": v(0, 31.75) * mm, "end": v(665.02, 31.75) * mm, "construction": true});
            skLineSegment(sketch, "E546.MirrorCS", {"start": v(216.63, 45.22) * mm, "end": v(216.63, 44.45) * mm});
            skLineSegment(sketch, "E547.MirrorCS", {"start": v(216.63, 43.7) * mm, "end": v(216.63, 44.45) * mm});
            skLineSegment(sketch, "E548.MirrorCS", {"start": v(184.5, 44.34) * mm, "end": v(184.5, 43.57) * mm});
            skLineSegment(sketch, "E549.MirrorCS", {"start": v(94.2, 61.1) * mm, "end": v(94.22, 60.34) * mm});
            skLineSegment(sketch, "E550.MirrorCS", {"start": v(48.46, 60.7) * mm, "end": v(48.47, 59.95) * mm});
            skLineSegment(sketch, "E551.MirrorCS", {"start": v(184.5, 44.34) * mm, "end": v(184.5, 45.1) * mm});
            skLineSegment(sketch, "E552.MirrorCS", {"start": v(216.63, 52.16) * mm, "end": v(216.63, 52.92) * mm});
            skLineSegment(sketch, "E553.MirrorCS", {"start": v(350.1, 52.98) * mm, "end": v(350.1, 53.74) * mm});
            skLineSegment(sketch, "E554.MirrorCS", {"start": v(356.44, 53.78) * mm, "end": v(356.45, 53.02) * mm});
            skLineSegment(sketch, "E555.MirrorCS", {"start": v(6.35, 43.68) * mm, "end": v(6.35, 42.92) * mm});
            skLineSegment(sketch, "E556.MirrorCS", {"start": v(325.9, 53.6) * mm, "end": v(325.91, 52.83) * mm});
            skLineSegment(sketch, "E557.MirrorCS", {"start": v(216.62, 53.69) * mm, "end": v(216.63, 52.92) * mm});
            skLineSegment(sketch, "E558.MirrorCS", {"start": v(54.82, 60) * mm, "end": v(54.81, 60.76) * mm});
            skLineSegment(sketch, "E559.MirrorCS", {"start": v(100.57, 60.4) * mm, "end": v(100.56, 61.16) * mm});
            skLineSegment(sketch, "E560.MirrorCS", {"start": v(325.91, 44.86) * mm, "end": v(325.91, 45.62) * mm});
            skLineSegment(sketch, "E561.MirrorCS", {"start": v(319.55, 54.32) * mm, "end": v(319.56, 53.56) * mm});
            skLineSegment(sketch, "E562.MirrorCS", {"start": v(540.1, 55.67) * mm, "end": v(540.1, 54.9) * mm});
            skLineSegment(sketch, "E563.MirrorCS", {"start": v(293.56, 53.4) * mm, "end": v(293.57, 52.63) * mm});
            skLineSegment(sketch, "E564.MirrorCS", {"start": v(94.22, 51.41) * mm, "end": v(94.22, 52.17) * mm});
            skLineSegment(sketch, "E565.MirrorCS", {"start": v(412.47, 45.18) * mm, "end": v(412.47, 45.94) * mm});
            skLineSegment(sketch, "E566.MirrorCS", {"start": v(520.87, 55.55) * mm, "end": v(520.87, 54.8) * mm});
            skLineSegment(sketch, "E567.MirrorCS", {"start": v(287.22, 52.6) * mm, "end": v(287.21, 53.36) * mm});
            skLineSegment(sketch, "E568.MirrorCS", {"start": v(546.46, 54.95) * mm, "end": v(546.46, 54.19) * mm});
            skLineSegment(sketch, "E569.MirrorCS", {"start": v(606.83, 56.08) * mm, "end": v(606.84, 55.32) * mm});
            skLineSegment(sketch, "E570.MirrorCS", {"start": v(613.2, 45.91) * mm, "end": v(613.2, 46.68) * mm});
            skLineSegment(sketch, "E571.MirrorCS", {"start": v(540.1, 54.15) * mm, "end": v(540.1, 54.9) * mm});
            skLineSegment(sketch, "E572.MirrorCS", {"start": v(184.5, 52.73) * mm, "end": v(184.5, 53.49) * mm});
            skLineSegment(sketch, "E573.MirrorCS", {"start": v(54.82, 51.93) * mm, "end": v(54.82, 51.17) * mm});
            skLineSegment(sketch, "E574.MirrorCS", {"start": v(184.5, 35.95) * mm, "end": v(184.5, 36.7) * mm});
            skLineSegment(sketch, "E575.MirrorCS", {"start": v(478.9, 44.66) * mm, "end": v(478.9, 45.42) * mm});
            skLineSegment(sketch, "E576.MirrorCS", {"start": v(178.14, 53.45) * mm, "end": v(178.15, 52.69) * mm});
            skLineSegment(sketch, "E577.MirrorCS", {"start": v(259.29, 53.19) * mm, "end": v(259.3, 52.42) * mm});
            skLineSegment(sketch, "E578.MirrorCS", {"start": v(48.47, 51.13) * mm, "end": v(48.47, 51.9) * mm});
            skLineSegment(sketch, "E579.MirrorCS", {"start": v(178.15, 36.7) * mm, "end": v(178.15, 35.94) * mm});
            skLineSegment(sketch, "E580.MirrorCS", {"start": v(48.47, 44.6) * mm, "end": v(48.47, 43.83) * mm});
            skLineSegment(sketch, "E581.MirrorCS", {"start": v(478.9, 55.3) * mm, "end": v(478.9, 54.53) * mm});
            skLineSegment(sketch, "E582.MirrorCS", {"start": v(606.84, 54.56) * mm, "end": v(606.84, 55.32) * mm});
            skLineSegment(sketch, "E583.MirrorCS", {"start": v(520.88, 54.03) * mm, "end": v(520.87, 54.8) * mm});
            skLineSegment(sketch, "E584.MirrorCS", {"start": v(6.35, 51.63) * mm, "end": v(6.35, 50.87) * mm});
            skLineSegment(sketch, "E585.MirrorCS", {"start": v(356.44, 53.78) * mm, "end": v(356.44, 54.54) * mm});
            skLineSegment(sketch, "E586.MirrorCS", {"start": v(54.82, 51.93) * mm, "end": v(54.81, 52.7) * mm});
            skLineSegment(sketch, "E587.MirrorCS", {"start": v(325.91, 44.86) * mm, "end": v(325.92, 44.1) * mm});
            skLineSegment(sketch, "E588.MirrorCS", {"start": v(137.4, 43.4) * mm, "end": v(137.4, 44.16) * mm});
            skLineSegment(sketch, "E589.MirrorCS", {"start": v(293.56, 44.74) * mm, "end": v(293.56, 45.5) * mm});
            skLineSegment(sketch, "E590.MirrorCS", {"start": v(6.35, 51.63) * mm, "end": v(6.35, 52.4) * mm});
            skLineSegment(sketch, "E591.MirrorCS", {"start": v(6.35, 59.59) * mm, "end": v(6.36, 58.82) * mm});
            skLineSegment(sketch, "E592.MirrorCS", {"start": v(48.48, 59.19) * mm, "end": v(48.47, 59.95) * mm});
            skLineSegment(sketch, "E593.MirrorCS", {"start": v(54.82, 60) * mm, "end": v(54.82, 59.24) * mm});
            skLineSegment(sketch, "E594.MirrorCS", {"start": v(94.22, 59.58) * mm, "end": v(94.22, 60.34) * mm});
            skLineSegment(sketch, "E595.MirrorCS", {"start": v(100.57, 60.4) * mm, "end": v(100.57, 59.63) * mm});
            skLineSegment(sketch, "E596.MirrorCS", {"start": v(350.09, 54.5) * mm, "end": v(350.1, 53.74) * mm});
            skLineSegment(sketch, "E597.MirrorCS", {"start": v(100.57, 44.03) * mm, "end": v(100.57, 43.26) * mm});
            skLineSegment(sketch, "E598.MirrorCS", {"start": v(178.15, 35.18) * mm, "end": v(178.15, 35.94) * mm});
            skLineSegment(sketch, "E599.MirrorCS", {"start": v(259.29, 53.19) * mm, "end": v(259.28, 53.95) * mm});
            skLineSegment(sketch, "E600.MirrorCS", {"start": v(378.92, 53.16) * mm, "end": v(378.91, 53.92) * mm});
            skLineSegment(sketch, "E601.MirrorCS", {"start": v(259.3, 44.61) * mm, "end": v(259.3, 43.85) * mm});
            skLineSegment(sketch, "E602.MirrorCS", {"start": v(412.47, 45.18) * mm, "end": v(412.47, 44.41) * mm});
            skLineSegment(sketch, "E603.MirrorCS", {"start": v(48.47, 43.07) * mm, "end": v(48.47, 43.83) * mm});
            skLineSegment(sketch, "E604.MirrorCS", {"start": v(478.9, 53.77) * mm, "end": v(478.9, 54.53) * mm});
            skLineSegment(sketch, "E605.MirrorCS", {"start": v(48.46, 52.65) * mm, "end": v(48.47, 51.9) * mm});
            skLineSegment(sketch, "E606.MirrorCS", {"start": v(222.98, 44.48) * mm, "end": v(222.98, 45.24) * mm});
            skLineSegment(sketch, "E607.MirrorCS", {"start": v(293.56, 44.74) * mm, "end": v(293.57, 43.98) * mm});
            skLineSegment(sketch, "E608.MirrorCS", {"start": v(325.9, 53.6) * mm, "end": v(325.9, 54.36) * mm});
            skLineSegment(sketch, "E609.MirrorCS", {"start": v(606.84, 46.65) * mm, "end": v(606.85, 45.9) * mm});
            skLineSegment(sketch, "E610.MirrorCS", {"start": v(184.5, 52.73) * mm, "end": v(184.5, 51.96) * mm});
            skLineSegment(sketch, "E611.MirrorCS", {"start": v(378.9, 54.68) * mm, "end": v(378.91, 53.92) * mm});
            skLineSegment(sketch, "E612.MirrorCS", {"start": v(94.21, 52.93) * mm, "end": v(94.22, 52.17) * mm});
            skLineSegment(sketch, "E613.MirrorCS", {"start": v(6.35, 43.68) * mm, "end": v(6.35, 44.44) * mm});
            skLineSegment(sketch, "E614.MirrorCS", {"start": v(6.35, 59.59) * mm, "end": v(6.34, 60.35) * mm});
            skLineSegment(sketch, "E615.MirrorCS", {"start": v(293.56, 53.4) * mm, "end": v(293.56, 54.16) * mm});
            skLineSegment(sketch, "E616.MirrorCS", {"start": v(54.82, 43.86) * mm, "end": v(54.82, 44.62) * mm});
            skLineSegment(sketch, "E617.MirrorCS", {"start": v(613.2, 45.91) * mm, "end": v(613.2, 45.15) * mm});
            skLineSegment(sketch, "E618.MirrorCS", {"start": v(287.2, 54.12) * mm, "end": v(287.21, 53.36) * mm});
            skLineSegment(sketch, "E619.MirrorCS", {"start": v(319.56, 52.8) * mm, "end": v(319.56, 53.56) * mm});
            skLineSegment(sketch, "E620.MirrorCS", {"start": v(478.9, 46.18) * mm, "end": v(478.9, 45.42) * mm});
            skLineSegment(sketch, "E621.MirrorCS", {"start": v(100.57, 44.03) * mm, "end": v(100.57, 44.79) * mm});
            skLineSegment(sketch, "E622.MirrorCS", {"start": v(222.98, 44.48) * mm, "end": v(222.98, 43.72) * mm});
            skLineSegment(sketch, "E623.MirrorCS", {"start": v(606.85, 45.13) * mm, "end": v(606.85, 45.9) * mm});
            skLineSegment(sketch, "E624.MirrorCS", {"start": v(259.3, 44.61) * mm, "end": v(259.29, 45.37) * mm});
            skLineSegment(sketch, "E625.MirrorCS", {"start": v(137.4, 44.92) * mm, "end": v(137.4, 44.16) * mm});
            skLineSegment(sketch, "E626.MirrorCS", {"start": v(581.74, 64.53) * mm, "end": v(581.73, 65.3) * mm});
            skLineSegment(sketch, "E627.MirrorCS", {"start": v(216.63, 60.63) * mm, "end": v(216.62, 61.4) * mm});
            skLineSegment(sketch, "E628.MirrorCS", {"start": v(94.22, 35.07) * mm, "end": v(94.22, 35.83) * mm});
            skLineSegment(sketch, "E629.MirrorCS", {"start": v(143.75, 44.19) * mm, "end": v(143.75, 44.95) * mm});
            skLineSegment(sketch, "E630.MirrorCS", {"start": v(575.4, 46.54) * mm, "end": v(575.4, 45.78) * mm});
            skLineSegment(sketch, "E631.MirrorCS", {"start": v(500.49, 55.43) * mm, "end": v(500.5, 54.67) * mm});
            skLineSegment(sketch, "E632.MirrorCS", {"start": v(438.14, 54.28) * mm, "end": v(438.15, 53.52) * mm});
            skLineSegment(sketch, "E633.MirrorCS", {"start": v(546.46, 54.95) * mm, "end": v(546.45, 55.7) * mm});
            skLineSegment(sketch, "E634.MirrorCS", {"start": v(462.38, 54.43) * mm, "end": v(462.37, 55.2) * mm});
            skLineSegment(sketch, "E635.MirrorCS", {"start": v(431.8, 53.48) * mm, "end": v(431.8, 54.24) * mm});
            skLineSegment(sketch, "E636.MirrorCS", {"start": v(575.38, 65.24) * mm, "end": v(575.39, 64.48) * mm});
            skLineSegment(sketch, "E637.MirrorCS", {"start": v(178.15, 43.55) * mm, "end": v(178.15, 44.31) * mm});
            skLineSegment(sketch, "E638.MirrorCS", {"start": v(431.79, 55) * mm, "end": v(431.8, 54.24) * mm});
            skLineSegment(sketch, "E639.MirrorCS", {"start": v(54.82, 35.79) * mm, "end": v(54.82, 35.02) * mm});
            skLineSegment(sketch, "E640.MirrorCS", {"start": v(485.25, 54.57) * mm, "end": v(485.25, 55.33) * mm});
            skLineSegment(sketch, "E641.MirrorCS", {"start": v(438.14, 54.28) * mm, "end": v(438.14, 55.04) * mm});
            skLineSegment(sketch, "E642.MirrorCS", {"start": v(412.47, 54.13) * mm, "end": v(412.47, 53.36) * mm});
            skLineSegment(sketch, "E643.MirrorCS", {"start": v(48.47, 35.02) * mm, "end": v(48.47, 35.78) * mm});
            skLineSegment(sketch, "E644.MirrorCS", {"start": v(456.03, 46.1) * mm, "end": v(456.03, 45.34) * mm});
            skLineSegment(sketch, "E645.MirrorCS", {"start": v(137.4, 36.65) * mm, "end": v(137.4, 35.89) * mm});
            skLineSegment(sketch, "E646.MirrorCS", {"start": v(385.26, 62.84) * mm, "end": v(385.25, 63.6) * mm});
            skLineSegment(sketch, "E647.MirrorCS", {"start": v(293.56, 62.05) * mm, "end": v(293.55, 62.82) * mm});
            skLineSegment(sketch, "E648.MirrorCS", {"start": v(385.26, 53.96) * mm, "end": v(385.27, 53.2) * mm});
            skLineSegment(sketch, "E649.MirrorCS", {"start": v(100.57, 52.21) * mm, "end": v(100.56, 52.97) * mm});
            skLineSegment(sketch, "E650.MirrorCS", {"start": v(456.03, 44.57) * mm, "end": v(456.03, 45.34) * mm});
            skLineSegment(sketch, "E651.MirrorCS", {"start": v(564.62, 45.74) * mm, "end": v(564.61, 46.5) * mm});
            skLineSegment(sketch, "E652.MirrorCS", {"start": v(100.57, 35.84) * mm, "end": v(100.57, 36.6) * mm});
            skLineSegment(sketch, "E653.MirrorCS", {"start": v(613.19, 55.36) * mm, "end": v(613.2, 54.6) * mm});
            skLineSegment(sketch, "E654.MirrorCS", {"start": v(252.94, 45.35) * mm, "end": v(252.94, 44.59) * mm});
            skLineSegment(sketch, "E655.MirrorCS", {"start": v(6.35, 35.73) * mm, "end": v(6.35, 34.96) * mm});
            skLineSegment(sketch, "E656.MirrorCS", {"start": v(54.82, 35.79) * mm, "end": v(54.82, 36.55) * mm});
            skLineSegment(sketch, "E657.MirrorCS", {"start": v(527.22, 54.83) * mm, "end": v(527.23, 54.07) * mm});
            skLineSegment(sketch, "E658.MirrorCS", {"start": v(143.75, 44.19) * mm, "end": v(143.75, 43.42) * mm});
            skLineSegment(sketch, "E659.MirrorCS", {"start": v(613.2, 46.68) * mm, "end": v(621.25, 46.7) * mm});
            skLineSegment(sketch, "E660.MirrorCS", {"start": v(94.22, 44.77) * mm, "end": v(94.22, 44) * mm});
            skLineSegment(sketch, "E661.MirrorCS", {"start": v(6.35, 35.73) * mm, "end": v(6.35, 36.49) * mm});
            skLineSegment(sketch, "E662.MirrorCS", {"start": v(184.5, 61.12) * mm, "end": v(184.5, 60.35) * mm});
            skLineSegment(sketch, "E663.MirrorCS", {"start": v(54.82, 43.86) * mm, "end": v(54.82, 43.1) * mm});
            skLineSegment(sketch, "E664.MirrorCS", {"start": v(485.25, 54.57) * mm, "end": v(485.26, 53.8) * mm});
            skLineSegment(sketch, "E665.MirrorCS", {"start": v(613.19, 55.36) * mm, "end": v(613.18, 56.12) * mm});
            skLineSegment(sketch, "E666.MirrorCS", {"start": v(178.15, 51.93) * mm, "end": v(178.15, 52.69) * mm});
            skLineSegment(sketch, "E667.MirrorCS", {"start": v(606.82, 65.5) * mm, "end": v(606.83, 64.75) * mm});
            skLineSegment(sketch, "E668.MirrorCS", {"start": v(520.85, 64.77) * mm, "end": v(520.86, 64) * mm});
            skLineSegment(sketch, "E669.MirrorCS", {"start": v(527.23, 45.6) * mm, "end": v(527.22, 46.36) * mm});
            skLineSegment(sketch, "E670.MirrorCS", {"start": v(184.5, 61.12) * mm, "end": v(184.49, 61.88) * mm});
            skLineSegment(sketch, "E671.MirrorCS", {"start": v(216.62, 62.15) * mm, "end": v(216.62, 61.4) * mm});
            skLineSegment(sketch, "E672.MirrorCS", {"start": v(178.15, 45.07) * mm, "end": v(178.15, 44.31) * mm});
            skLineSegment(sketch, "E673.MirrorCS", {"start": v(438.15, 45.27) * mm, "end": v(438.14, 46.03) * mm});
            skLineSegment(sketch, "E674.MirrorCS", {"start": v(564.6, 64.38) * mm, "end": v(564.6, 63.62) * mm});
            skLineSegment(sketch, "E675.MirrorCS", {"start": v(621.26, 45.18) * mm, "end": v(621.26, 45.94) * mm});
            skLineSegment(sketch, "E676.MirrorCS", {"start": v(527.22, 54.83) * mm, "end": v(527.22, 55.6) * mm});
            skLineSegment(sketch, "E677.MirrorCS", {"start": v(581.75, 55.16) * mm, "end": v(581.75, 54.4) * mm});
            skLineSegment(sketch, "E678.MirrorCS", {"start": v(143.75, 35.9) * mm, "end": v(143.75, 36.66) * mm});
            skLineSegment(sketch, "E679.MirrorCS", {"start": v(94.22, 43.24) * mm, "end": v(94.22, 44) * mm});
            skLineSegment(sketch, "E680.MirrorCS", {"start": v(143.75, 52.48) * mm, "end": v(143.74, 53.24) * mm});
            skLineSegment(sketch, "E681.MirrorCS", {"start": v(575.4, 55.89) * mm, "end": v(575.4, 55.13) * mm});
            skLineSegment(sketch, "E682.MirrorCS", {"start": v(500.5, 53.9) * mm, "end": v(500.5, 54.67) * mm});
            skLineSegment(sketch, "E683.MirrorCS", {"start": v(184.5, 35.95) * mm, "end": v(184.5, 35.18) * mm});
            skLineSegment(sketch, "E684.MirrorCS", {"start": v(520.87, 46.34) * mm, "end": v(520.88, 45.57) * mm});
            skLineSegment(sketch, "E685.MirrorCS", {"start": v(412.47, 54.13) * mm, "end": v(412.46, 54.89) * mm});
            skLineSegment(sketch, "E686.MirrorCS", {"start": v(293.56, 62.05) * mm, "end": v(293.56, 61.3) * mm});
            skLineSegment(sketch, "E687.MirrorCS", {"start": v(438.13, 63.3) * mm, "end": v(438.14, 62.53) * mm});
            skLineSegment(sketch, "E688.MirrorCS", {"start": v(252.94, 43.83) * mm, "end": v(252.94, 44.59) * mm});
            skLineSegment(sketch, "E689.MirrorCS", {"start": v(406.12, 44.39) * mm, "end": v(406.12, 45.15) * mm});
            skLineSegment(sketch, "E690.MirrorCS", {"start": v(527.23, 45.6) * mm, "end": v(527.23, 44.84) * mm});
            skLineSegment(sketch, "E691.MirrorCS", {"start": v(613.2, 45.15) * mm, "end": v(621.26, 45.18) * mm});
            skLineSegment(sketch, "E692.MirrorCS", {"start": v(575.4, 54.36) * mm, "end": v(575.4, 55.13) * mm});
            skLineSegment(sketch, "E693.MirrorCS", {"start": v(438.13, 63.3) * mm, "end": v(438.13, 64.06) * mm});
            skLineSegment(sketch, "E694.MirrorCS", {"start": v(178.14, 61.82) * mm, "end": v(178.15, 61.06) * mm});
            skLineSegment(sketch, "E695.MirrorCS", {"start": v(143.75, 52.48) * mm, "end": v(143.75, 51.71) * mm});
            skLineSegment(sketch, "E696.MirrorCS", {"start": v(94.22, 36.6) * mm, "end": v(94.22, 35.83) * mm});
            skLineSegment(sketch, "E697.MirrorCS", {"start": v(143.75, 35.9) * mm, "end": v(143.75, 35.13) * mm});
            skLineSegment(sketch, "E698.MirrorCS", {"start": v(385.26, 53.96) * mm, "end": v(385.26, 54.72) * mm});
            skLineSegment(sketch, "E699.MirrorCS", {"start": v(462.38, 54.43) * mm, "end": v(462.38, 53.67) * mm});
            skLineSegment(sketch, "E700.MirrorCS", {"start": v(591.55, 65.38) * mm, "end": v(591.56, 64.61) * mm});
            skLineSegment(sketch, "E701.MirrorCS", {"start": v(137.4, 35.13) * mm, "end": v(137.4, 35.89) * mm});
            skLineSegment(sketch, "E702.MirrorCS", {"start": v(406.12, 45.91) * mm, "end": v(406.12, 45.15) * mm});
            skLineSegment(sketch, "E703.MirrorCS", {"start": v(520.88, 44.81) * mm, "end": v(520.88, 45.57) * mm});
            skLineSegment(sketch, "E704.MirrorCS", {"start": v(564.61, 55.06) * mm, "end": v(564.62, 54.3) * mm});
            skLineSegment(sketch, "E705.MirrorCS", {"start": v(520.87, 63.24) * mm, "end": v(520.86, 64) * mm});
            skLineSegment(sketch, "E706.MirrorCS", {"start": v(621.25, 46.7) * mm, "end": v(621.26, 45.94) * mm});
            skLineSegment(sketch, "E707.MirrorCS", {"start": v(100.57, 52.21) * mm, "end": v(100.57, 51.45) * mm});
            skLineSegment(sketch, "E708.MirrorCS", {"start": v(385.26, 62.84) * mm, "end": v(385.26, 62.08) * mm});
            skLineSegment(sketch, "E709.MirrorCS", {"start": v(606.83, 63.98) * mm, "end": v(606.83, 64.75) * mm});
            skLineSegment(sketch, "E710.MirrorCS", {"start": v(100.57, 35.84) * mm, "end": v(100.57, 35.08) * mm});
            skLineSegment(sketch, "E711.MirrorCS", {"start": v(558.27, 54.26) * mm, "end": v(558.26, 55.02) * mm});
            skLineSegment(sketch, "E712.MirrorCS", {"start": v(558.26, 55.78) * mm, "end": v(558.26, 55.02) * mm});
            skLineSegment(sketch, "E713.MirrorCS", {"start": v(378.91, 62.03) * mm, "end": v(378.9, 62.79) * mm});
            skLineSegment(sketch, "E714.MirrorCS", {"start": v(506.83, 63.89) * mm, "end": v(506.84, 63.12) * mm});
            skLineSegment(sketch, "E715.MirrorCS", {"start": v(597.92, 63.9) * mm, "end": v(606.83, 63.98) * mm});
            skLineSegment(sketch, "E716.MirrorCS", {"start": v(293.57, 36.08) * mm, "end": v(293.57, 35.32) * mm});
            skLineSegment(sketch, "E717.MirrorCS", {"start": v(500.5, 44.74) * mm, "end": v(500.5, 45.5) * mm});
            skLineSegment(sketch, "E718.MirrorCS", {"start": v(597.93, 45.86) * mm, "end": v(597.93, 45.1) * mm});
            skLineSegment(sketch, "E719.MirrorCS", {"start": v(222.98, 52.96) * mm, "end": v(222.97, 53.72) * mm});
            skLineSegment(sketch, "E720.MirrorCS", {"start": v(259.28, 61.76) * mm, "end": v(259.28, 62.52) * mm});
            skLineSegment(sketch, "E721.MirrorCS", {"start": v(597.93, 45.86) * mm, "end": v(597.93, 46.62) * mm});
            skLineSegment(sketch, "E722.MirrorCS", {"start": v(356.45, 44.97) * mm, "end": v(356.45, 44.2) * mm});
            skLineSegment(sketch, "E723.MirrorCS", {"start": v(143.75, 60.77) * mm, "end": v(143.74, 61.53) * mm});
            skLineSegment(sketch, "E724.MirrorCS", {"start": v(500.49, 63.07) * mm, "end": v(500.48, 63.83) * mm});
            skLineSegment(sketch, "E725.MirrorCS", {"start": v(597.91, 64.67) * mm, "end": v(597.92, 63.9) * mm});
            skLineSegment(sketch, "E726.MirrorCS", {"start": v(325.9, 62.33) * mm, "end": v(325.9, 63.1) * mm});
            skLineSegment(sketch, "E727.MirrorCS", {"start": v(597.93, 46.62) * mm, "end": v(606.84, 46.65) * mm});
            skLineSegment(sketch, "E728.MirrorCS", {"start": v(350.1, 45.7) * mm, "end": v(350.1, 44.95) * mm});
            skLineSegment(sketch, "E729.MirrorCS", {"start": v(485.26, 45.44) * mm, "end": v(485.26, 44.68) * mm});
            skLineSegment(sketch, "E730.MirrorCS", {"start": v(581.74, 55.93) * mm, "end": v(591.57, 55.99) * mm});
            skLineSegment(sketch, "E731.MirrorCS", {"start": v(591.57, 63.85) * mm, "end": v(591.56, 64.61) * mm});
            skLineSegment(sketch, "E732.MirrorCS", {"start": v(597.91, 64.67) * mm, "end": v(597.9, 65.43) * mm});
            skLineSegment(sketch, "E733.MirrorCS", {"start": v(350.1, 44.18) * mm, "end": v(350.1, 44.95) * mm});
            skLineSegment(sketch, "E734.MirrorCS", {"start": v(581.75, 45.8) * mm, "end": v(581.76, 45.04) * mm});
            skLineSegment(sketch, "E735.MirrorCS", {"start": v(621.25, 54.64) * mm, "end": v(621.25, 55.4) * mm});
            skLineSegment(sketch, "E736.MirrorCS", {"start": v(597.9, 65.43) * mm, "end": v(606.82, 65.5) * mm});
            skLineSegment(sketch, "E737.MirrorCS", {"start": v(485.24, 63.7) * mm, "end": v(485.25, 62.94) * mm});
            skLineSegment(sketch, "E738.MirrorCS", {"start": v(581.74, 63.77) * mm, "end": v(591.57, 63.85) * mm});
            skLineSegment(sketch, "E739.MirrorCS", {"start": v(613.18, 64.8) * mm, "end": v(613.17, 65.56) * mm});
            skLineSegment(sketch, "E740.MirrorCS", {"start": v(506.85, 45.52) * mm, "end": v(506.84, 46.28) * mm});
            skLineSegment(sketch, "E741.MirrorCS", {"start": v(287.21, 45.48) * mm, "end": v(287.21, 44.71) * mm});
            skLineSegment(sketch, "E742.MirrorCS", {"start": v(558.27, 46.47) * mm, "end": v(558.27, 45.71) * mm});
            skLineSegment(sketch, "E743.MirrorCS", {"start": v(558.27, 44.95) * mm, "end": v(558.27, 45.71) * mm});
            skLineSegment(sketch, "E744.MirrorCS", {"start": v(216.63, 35.22) * mm, "end": v(216.63, 35.98) * mm});
            skLineSegment(sketch, "E745.MirrorCS", {"start": v(564.6, 63.62) * mm, "end": v(575.4, 63.71) * mm});
            skLineSegment(sketch, "E746.MirrorCS", {"start": v(325.9, 62.33) * mm, "end": v(325.91, 61.57) * mm});
            skLineSegment(sketch, "E747.MirrorCS", {"start": v(222.98, 52.96) * mm, "end": v(222.98, 52.2) * mm});
            skLineSegment(sketch, "E748.MirrorCS", {"start": v(621.24, 56.17) * mm, "end": v(621.25, 55.4) * mm});
            skLineSegment(sketch, "E749.MirrorCS", {"start": v(319.57, 44.07) * mm, "end": v(319.56, 44.83) * mm});
            skLineSegment(sketch, "E750.MirrorCS", {"start": v(564.61, 46.5) * mm, "end": v(575.4, 46.54) * mm});
            skLineSegment(sketch, "E751.MirrorCS", {"start": v(564.62, 45.74) * mm, "end": v(564.62, 44.97) * mm});
            skLineSegment(sketch, "E752.MirrorCS", {"start": v(575.4, 63.71) * mm, "end": v(575.39, 64.48) * mm});
            skLineSegment(sketch, "E753.MirrorCS", {"start": v(378.9, 63.55) * mm, "end": v(378.9, 62.79) * mm});
            skLineSegment(sketch, "E754.MirrorCS", {"start": v(406.11, 54.85) * mm, "end": v(406.12, 54.09) * mm});
            skLineSegment(sketch, "E755.MirrorCS", {"start": v(462.38, 45.36) * mm, "end": v(462.38, 44.6) * mm});
            skLineSegment(sketch, "E756.MirrorCS", {"start": v(385.27, 45.07) * mm, "end": v(385.27, 45.84) * mm});
            skLineSegment(sketch, "E757.MirrorCS", {"start": v(564.62, 44.97) * mm, "end": v(575.4, 45.01) * mm});
            skLineSegment(sketch, "E758.MirrorCS", {"start": v(581.74, 64.53) * mm, "end": v(581.74, 63.77) * mm});
            skLineSegment(sketch, "E759.MirrorCS", {"start": v(478.9, 62.88) * mm, "end": v(478.9, 63.65) * mm});
            skLineSegment(sketch, "E760.MirrorCS", {"start": v(527.21, 64.06) * mm, "end": v(527.2, 64.82) * mm});
            skLineSegment(sketch, "E761.MirrorCS", {"start": v(506.83, 63.89) * mm, "end": v(506.83, 64.65) * mm});
            skLineSegment(sketch, "E762.MirrorCS", {"start": v(406.12, 53.32) * mm, "end": v(406.12, 54.09) * mm});
            skLineSegment(sketch, "E763.MirrorCS", {"start": v(252.94, 52.38) * mm, "end": v(252.94, 53.15) * mm});
            skLineSegment(sketch, "E764.MirrorCS", {"start": v(591.57, 55.99) * mm, "end": v(591.57, 55.22) * mm});
            skLineSegment(sketch, "E765.MirrorCS", {"start": v(613.2, 54.6) * mm, "end": v(621.25, 54.64) * mm});
            skLineSegment(sketch, "E766.MirrorCS", {"start": v(378.92, 45.81) * mm, "end": v(378.92, 45.05) * mm});
            skLineSegment(sketch, "E767.MirrorCS", {"start": v(575.4, 45.01) * mm, "end": v(575.4, 45.78) * mm});
            skLineSegment(sketch, "E768.MirrorCS", {"start": v(178.15, 60.3) * mm, "end": v(178.15, 61.06) * mm});
            skLineSegment(sketch, "E769.MirrorCS", {"start": v(143.75, 60.77) * mm, "end": v(143.75, 60) * mm});
            skLineSegment(sketch, "E770.MirrorCS", {"start": v(431.8, 46) * mm, "end": v(431.8, 45.25) * mm});
            skLineSegment(sketch, "E771.MirrorCS", {"start": v(540.11, 44.88) * mm, "end": v(540.11, 45.65) * mm});
            skLineSegment(sketch, "E772.MirrorCS", {"start": v(597.92, 56.03) * mm, "end": v(606.83, 56.08) * mm});
            skLineSegment(sketch, "E773.MirrorCS", {"start": v(431.78, 64) * mm, "end": v(431.78, 63.24) * mm});
            skLineSegment(sketch, "E774.MirrorCS", {"start": v(581.75, 54.4) * mm, "end": v(591.58, 54.46) * mm});
            skLineSegment(sketch, "E775.MirrorCS", {"start": v(546.45, 64.23) * mm, "end": v(546.44, 64.99) * mm});
            skLineSegment(sketch, "E776.MirrorCS", {"start": v(546.45, 64.23) * mm, "end": v(546.45, 63.46) * mm});
            skLineSegment(sketch, "E777.MirrorCS", {"start": v(581.73, 65.3) * mm, "end": v(591.55, 65.38) * mm});
            skLineSegment(sketch, "E778.MirrorCS", {"start": v(597.93, 54.5) * mm, "end": v(606.84, 54.56) * mm});
            skLineSegment(sketch, "E779.MirrorCS", {"start": v(581.75, 55.16) * mm, "end": v(581.74, 55.93) * mm});
            skLineSegment(sketch, "E780.MirrorCS", {"start": v(137.4, 53.2) * mm, "end": v(137.4, 52.44) * mm});
            skLineSegment(sketch, "E781.MirrorCS", {"start": v(506.84, 54.7) * mm, "end": v(506.85, 53.94) * mm});
            skLineSegment(sketch, "E782.MirrorCS", {"start": v(485.26, 45.44) * mm, "end": v(485.25, 46.2) * mm});
            skLineSegment(sketch, "E783.MirrorCS", {"start": v(564.6, 64.38) * mm, "end": v(564.6, 65.14) * mm});
            skLineSegment(sketch, "E784.MirrorCS", {"start": v(564.6, 65.14) * mm, "end": v(575.38, 65.24) * mm});
            skLineSegment(sketch, "E785.MirrorCS", {"start": v(319.56, 61.52) * mm, "end": v(319.55, 62.28) * mm});
            skLineSegment(sketch, "E786.MirrorCS", {"start": v(456.02, 62.69) * mm, "end": v(456.02, 63.45) * mm});
            skLineSegment(sketch, "E787.MirrorCS", {"start": v(506.84, 54.7) * mm, "end": v(506.84, 55.47) * mm});
            skLineSegment(sketch, "E788.MirrorCS", {"start": v(540.1, 46.4) * mm, "end": v(540.11, 45.65) * mm});
            skLineSegment(sketch, "E789.MirrorCS", {"start": v(319.56, 45.6) * mm, "end": v(319.56, 44.83) * mm});
            skLineSegment(sketch, "E790.MirrorCS", {"start": v(500.5, 46.26) * mm, "end": v(500.5, 45.5) * mm});
            skLineSegment(sketch, "E791.MirrorCS", {"start": v(438.15, 45.27) * mm, "end": v(438.15, 44.5) * mm});
            skLineSegment(sketch, "E792.MirrorCS", {"start": v(597.92, 55.26) * mm, "end": v(597.93, 54.5) * mm});
            skLineSegment(sketch, "E793.MirrorCS", {"start": v(558.24, 65.1) * mm, "end": v(558.25, 64.33) * mm});
            skLineSegment(sketch, "E794.MirrorCS", {"start": v(456.01, 64.21) * mm, "end": v(456.02, 63.45) * mm});
            skLineSegment(sketch, "E795.MirrorCS", {"start": v(558.26, 63.57) * mm, "end": v(558.25, 64.33) * mm});
            skLineSegment(sketch, "E796.MirrorCS", {"start": v(462.38, 45.36) * mm, "end": v(462.38, 46.12) * mm});
            skLineSegment(sketch, "E797.MirrorCS", {"start": v(546.46, 45.67) * mm, "end": v(546.46, 44.9) * mm});
            skLineSegment(sketch, "E798.MirrorCS", {"start": v(546.46, 45.67) * mm, "end": v(546.46, 46.43) * mm});
            skLineSegment(sketch, "E799.MirrorCS", {"start": v(287.22, 43.95) * mm, "end": v(287.21, 44.71) * mm});
            skLineSegment(sketch, "E800.MirrorCS", {"start": v(431.8, 44.48) * mm, "end": v(431.8, 45.25) * mm});
            skLineSegment(sketch, "E801.MirrorCS", {"start": v(591.58, 54.46) * mm, "end": v(591.57, 55.22) * mm});
            skLineSegment(sketch, "E802.MirrorCS", {"start": v(597.92, 55.26) * mm, "end": v(597.92, 56.03) * mm});
            skLineSegment(sketch, "E803.MirrorCS", {"start": v(319.55, 63.04) * mm, "end": v(319.55, 62.28) * mm});
            skLineSegment(sketch, "E804.MirrorCS", {"start": v(500.48, 64.6) * mm, "end": v(500.48, 63.83) * mm});
            skLineSegment(sketch, "E805.MirrorCS", {"start": v(506.85, 45.52) * mm, "end": v(506.85, 44.76) * mm});
            skLineSegment(sketch, "E806.MirrorCS", {"start": v(48.47, 36.54) * mm, "end": v(48.47, 35.78) * mm});
            skLineSegment(sketch, "E807.MirrorCS", {"start": v(597.93, 45.1) * mm, "end": v(606.85, 45.13) * mm});
            skLineSegment(sketch, "E808.MirrorCS", {"start": v(613.18, 56.12) * mm, "end": v(621.24, 56.17) * mm});
            skLineSegment(sketch, "E809.MirrorCS", {"start": v(456.02, 55.15) * mm, "end": v(456.03, 54.4) * mm});
            skLineSegment(sketch, "E810.MirrorCS", {"start": v(485.24, 63.7) * mm, "end": v(485.24, 64.46) * mm});
            skLineSegment(sketch, "E811.MirrorCS", {"start": v(259.28, 61.76) * mm, "end": v(259.29, 61) * mm});
            skLineSegment(sketch, "E812.MirrorCS", {"start": v(591.58, 46.6) * mm, "end": v(591.58, 45.83) * mm});
            skLineSegment(sketch, "E813.MirrorCS", {"start": v(252.93, 53.9) * mm, "end": v(252.94, 53.15) * mm});
            skLineSegment(sketch, "E814.MirrorCS", {"start": v(564.62, 54.3) * mm, "end": v(575.4, 54.36) * mm});
            skLineSegment(sketch, "E815.MirrorCS", {"start": v(137.4, 51.68) * mm, "end": v(137.4, 52.44) * mm});
            skLineSegment(sketch, "E816.MirrorCS", {"start": v(527.21, 64.06) * mm, "end": v(527.22, 63.3) * mm});
            skLineSegment(sketch, "E817.MirrorCS", {"start": v(293.57, 36.08) * mm, "end": v(293.56, 36.84) * mm});
            skLineSegment(sketch, "E818.MirrorCS", {"start": v(356.45, 44.97) * mm, "end": v(356.44, 45.73) * mm});
            skLineSegment(sketch, "E819.MirrorCS", {"start": v(456.03, 53.63) * mm, "end": v(456.03, 54.4) * mm});
            skLineSegment(sketch, "E820.MirrorCS", {"start": v(613.18, 64.8) * mm, "end": v(613.18, 64.04) * mm});
            skLineSegment(sketch, "E821.MirrorCS", {"start": v(216.63, 36.75) * mm, "end": v(216.63, 35.98) * mm});
            skLineSegment(sketch, "E822.MirrorCS", {"start": v(385.27, 45.07) * mm, "end": v(385.27, 44.31) * mm});
            skLineSegment(sketch, "E823.MirrorCS", {"start": v(564.6, 55.82) * mm, "end": v(575.4, 55.89) * mm});
            skLineSegment(sketch, "E824.MirrorCS", {"start": v(564.61, 55.06) * mm, "end": v(564.6, 55.82) * mm});
            skLineSegment(sketch, "E825.MirrorCS", {"start": v(478.89, 64.4) * mm, "end": v(478.9, 63.65) * mm});
            skLineSegment(sketch, "E826.MirrorCS", {"start": v(581.75, 45.8) * mm, "end": v(581.75, 46.56) * mm});
            skLineSegment(sketch, "E827.MirrorCS", {"start": v(378.92, 44.29) * mm, "end": v(378.92, 45.05) * mm});
            skLineSegment(sketch, "E828.MirrorCS", {"start": v(222.98, 36) * mm, "end": v(222.98, 36.75) * mm});
            skLineSegment(sketch, "E829.MirrorCS", {"start": v(137.4, 61.47) * mm, "end": v(137.4, 60.71) * mm});
            skLineSegment(sketch, "E830.MirrorCS", {"start": v(591.58, 45.07) * mm, "end": v(591.58, 45.83) * mm});
            skLineSegment(sketch, "E831.MirrorCS", {"start": v(287.22, 35.3) * mm, "end": v(287.22, 36.07) * mm});
            skLineSegment(sketch, "E832.MirrorCS", {"start": v(581.76, 45.04) * mm, "end": v(591.58, 45.07) * mm});
            skLineSegment(sketch, "E833.MirrorCS", {"start": v(412.46, 63.08) * mm, "end": v(412.45, 63.84) * mm});
            skLineSegment(sketch, "E834.MirrorCS", {"start": v(356.44, 62.6) * mm, "end": v(356.44, 61.83) * mm});
            skLineSegment(sketch, "E835.MirrorCS", {"start": v(350.08, 63.3) * mm, "end": v(350.09, 62.54) * mm});
            skLineSegment(sketch, "E836.MirrorCS", {"start": v(259.3, 36.04) * mm, "end": v(259.3, 35.28) * mm});
            skLineSegment(sketch, "E837.MirrorCS", {"start": v(259.3, 36.04) * mm, "end": v(259.3, 36.8) * mm});
            skLineSegment(sketch, "E838.MirrorCS", {"start": v(462.37, 63.5) * mm, "end": v(462.37, 62.74) * mm});
            skLineSegment(sketch, "E839.MirrorCS", {"start": v(252.93, 62.47) * mm, "end": v(252.93, 61.7) * mm});
            skLineSegment(sketch, "E840.MirrorCS", {"start": v(222.98, 36) * mm, "end": v(222.98, 35.23) * mm});
            skLineSegment(sketch, "E841.MirrorCS", {"start": v(613.17, 65.56) * mm, "end": v(621.23, 65.63) * mm});
            skLineSegment(sketch, "E842.MirrorCS", {"start": v(350.1, 61.78) * mm, "end": v(350.09, 62.54) * mm});
            skLineSegment(sketch, "E843.MirrorCS", {"start": v(252.94, 35.27) * mm, "end": v(252.94, 36.03) * mm});
            skLineSegment(sketch, "E844.MirrorCS", {"start": v(137.4, 59.95) * mm, "end": v(137.4, 60.71) * mm});
            skLineSegment(sketch, "E845.MirrorCS", {"start": v(581.75, 46.56) * mm, "end": v(591.58, 46.6) * mm});
            skLineSegment(sketch, "E846.MirrorCS", {"start": v(462.37, 63.5) * mm, "end": v(462.36, 64.27) * mm});
            skLineSegment(sketch, "E847.MirrorCS", {"start": v(431.8, 62.48) * mm, "end": v(431.78, 63.24) * mm});
            skLineSegment(sketch, "E848.MirrorCS", {"start": v(287.21, 61.24) * mm, "end": v(287.2, 62) * mm});
            skLineSegment(sketch, "E849.MirrorCS", {"start": v(540.1, 63.41) * mm, "end": v(540.1, 64.17) * mm});
            skLineSegment(sketch, "E850.MirrorCS", {"start": v(287.2, 62.76) * mm, "end": v(287.2, 62) * mm});
            skLineSegment(sketch, "E851.MirrorCS", {"start": v(222.97, 61.45) * mm, "end": v(222.97, 62.2) * mm});
            skLineSegment(sketch, "E852.MirrorCS", {"start": v(540.09, 64.93) * mm, "end": v(540.1, 64.17) * mm});
            skLineSegment(sketch, "E853.MirrorCS", {"start": v(412.46, 63.08) * mm, "end": v(412.46, 62.31) * mm});
            skLineSegment(sketch, "E854.MirrorCS", {"start": v(621.24, 64.1) * mm, "end": v(621.24, 64.87) * mm});
            skLineSegment(sketch, "E855.MirrorCS", {"start": v(406.12, 62.26) * mm, "end": v(406.1, 63.02) * mm});
            skLineSegment(sketch, "E856.MirrorCS", {"start": v(613.18, 64.04) * mm, "end": v(621.24, 64.1) * mm});
            skLineSegment(sketch, "E857.MirrorCS", {"start": v(252.94, 60.94) * mm, "end": v(252.93, 61.7) * mm});
            skLineSegment(sketch, "E858.MirrorCS", {"start": v(252.94, 36.8) * mm, "end": v(252.94, 36.03) * mm});
            skLineSegment(sketch, "E859.MirrorCS", {"start": v(356.44, 62.6) * mm, "end": v(356.43, 63.36) * mm});
            skLineSegment(sketch, "E860.MirrorCS", {"start": v(406.1, 63.78) * mm, "end": v(406.1, 63.02) * mm});
            skLineSegment(sketch, "E861.MirrorCS", {"start": v(621.23, 65.63) * mm, "end": v(621.24, 64.87) * mm});
            skLineSegment(sketch, "E862.MirrorCS", {"start": v(222.97, 61.45) * mm, "end": v(222.98, 60.69) * mm});
            skLineSegment(sketch, "E863.MirrorCS", {"start": v(287.21, 36.83) * mm, "end": v(287.22, 36.07) * mm});
            skLineSegment(sketch, "E864.MirrorCS", {"start": v(406.12, 36.98) * mm, "end": v(406.12, 36.22) * mm});
            skLineSegment(sketch, "E865.MirrorCS", {"start": v(325.92, 36.12) * mm, "end": v(325.91, 36.88) * mm});
            skLineSegment(sketch, "E866.MirrorCS", {"start": v(184.5, 51.96) * mm, "end": v(216.63, 52.16) * mm, "construction": true});
            skLineSegment(sketch, "E867.MirrorCS", {"start": v(356.45, 36.16) * mm, "end": v(356.45, 35.4) * mm});
            skLineSegment(sketch, "E868.MirrorCS", {"start": v(350.1, 35.39) * mm, "end": v(350.1, 36.15) * mm});
            skLineSegment(sketch, "E869.MirrorCS", {"start": v(385.27, 36.2) * mm, "end": v(385.27, 36.95) * mm});
            skLineSegment(sketch, "E870.MirrorCS", {"start": v(325.92, 36.12) * mm, "end": v(325.92, 35.36) * mm});
            skLineSegment(sketch, "E871.MirrorCS", {"start": v(293.57, 52.63) * mm, "end": v(319.56, 52.8) * mm});
            skLineSegment(sketch, "E872.MirrorCS", {"start": v(319.56, 36.87) * mm, "end": v(319.57, 36.11) * mm});
            skLineSegment(sketch, "E873.MirrorCS", {"start": v(184.5, 43.57) * mm, "end": v(216.63, 43.7) * mm, "construction": true});
            skLineSegment(sketch, "E874.MirrorCS", {"start": v(325.9, 54.36) * mm, "end": v(350.09, 54.5) * mm});
            skLineSegment(sketch, "E875.MirrorCS", {"start": v(6.34, 60.35) * mm, "end": v(48.46, 60.7) * mm});
            skLineSegment(sketch, "E876.MirrorCS", {"start": v(184.5, 53.49) * mm, "end": v(216.62, 53.69) * mm, "construction": true});
            skLineSegment(sketch, "E877.MirrorCS", {"start": v(259.3, 52.42) * mm, "end": v(287.22, 52.6) * mm});
            skLineSegment(sketch, "E878.MirrorCS", {"start": v(54.81, 60.76) * mm, "end": v(94.2, 61.1) * mm});
            skLineSegment(sketch, "E879.MirrorCS", {"start": v(184.5, 36.7) * mm, "end": v(216.63, 36.75) * mm, "construction": true});
            skLineSegment(sketch, "E880.MirrorCS", {"start": v(356.45, 36.16) * mm, "end": v(356.45, 36.92) * mm});
            skLineSegment(sketch, "E881.MirrorCS", {"start": v(184.5, 60.35) * mm, "end": v(216.63, 60.63) * mm, "construction": true});
            skLineSegment(sketch, "E882.MirrorCS", {"start": v(184.5, 45.1) * mm, "end": v(216.63, 45.22) * mm, "construction": true});
            skLineSegment(sketch, "E883.MirrorCS", {"start": v(350.1, 36.91) * mm, "end": v(350.1, 36.15) * mm});
            skLineSegment(sketch, "E884.MirrorCS", {"start": v(184.5, 35.18) * mm, "end": v(216.63, 35.22) * mm, "construction": true});
            skLineSegment(sketch, "E885.MirrorCS", {"start": v(356.45, 53.02) * mm, "end": v(378.92, 53.16) * mm});
            skLineSegment(sketch, "E886.MirrorCS", {"start": v(412.47, 36.23) * mm, "end": v(412.47, 36.99) * mm});
            skLineSegment(sketch, "E887.MirrorCS", {"start": v(378.92, 36.95) * mm, "end": v(378.92, 36.18) * mm});
            skLineSegment(sketch, "E888.MirrorCS", {"start": v(319.57, 35.35) * mm, "end": v(319.57, 36.11) * mm});
            skLineSegment(sketch, "E889.MirrorCS", {"start": v(293.57, 35.32) * mm, "end": v(319.57, 35.35) * mm});
            skLineSegment(sketch, "E890.MirrorCS", {"start": v(438.15, 53.52) * mm, "end": v(456.03, 53.63) * mm});
            skLineSegment(sketch, "E891.MirrorCS", {"start": v(6.35, 44.44) * mm, "end": v(48.47, 44.6) * mm});
            skLineSegment(sketch, "E892.MirrorCS", {"start": v(356.45, 44.2) * mm, "end": v(378.92, 44.29) * mm});
            skLineSegment(sketch, "E893.MirrorCS", {"start": v(546.46, 54.19) * mm, "end": v(558.27, 54.26) * mm});
            skLineSegment(sketch, "E894.MirrorCS", {"start": v(546.46, 46.43) * mm, "end": v(558.27, 46.47) * mm});
            skLineSegment(sketch, "E895.MirrorCS", {"start": v(54.82, 44.62) * mm, "end": v(94.22, 44.77) * mm});
            skLineSegment(sketch, "E896.MirrorCS", {"start": v(485.26, 44.68) * mm, "end": v(500.5, 44.74) * mm});
            skLineSegment(sketch, "E897.MirrorCS", {"start": v(54.82, 51.17) * mm, "end": v(94.22, 51.41) * mm});
            skLineSegment(sketch, "E898.MirrorCS", {"start": v(356.44, 61.83) * mm, "end": v(378.91, 62.03) * mm});
            skLineSegment(sketch, "E899.MirrorCS", {"start": v(325.91, 36.88) * mm, "end": v(350.1, 36.91) * mm});
            skLineSegment(sketch, "E900.MirrorCS", {"start": v(143.75, 44.95) * mm, "end": v(178.15, 45.07) * mm});
            skLineSegment(sketch, "E901.MirrorCS", {"start": v(184.5, 43.57) * mm, "end": v(216.63, 43.7) * mm});
            skLineSegment(sketch, "E902.MirrorCS", {"start": v(462.37, 55.2) * mm, "end": v(478.9, 55.3) * mm});
            skLineSegment(sketch, "E903.MirrorCS", {"start": v(412.47, 53.36) * mm, "end": v(431.8, 53.48) * mm});
            skLineSegment(sketch, "E904.MirrorCS", {"start": v(546.44, 64.99) * mm, "end": v(558.24, 65.1) * mm});
            skLineSegment(sketch, "E905.MirrorCS", {"start": v(485.25, 62.94) * mm, "end": v(500.49, 63.07) * mm});
            skLineSegment(sketch, "E906.MirrorCS", {"start": v(462.38, 37.05) * mm, "end": v(478.9, 37.07) * mm});
            skLineSegment(sketch, "E907.MirrorCS", {"start": v(259.3, 35.28) * mm, "end": v(287.22, 35.3) * mm});
            skLineSegment(sketch, "E908.MirrorCS", {"start": v(143.75, 43.42) * mm, "end": v(178.15, 43.55) * mm});
            skLineSegment(sketch, "E909.MirrorCS", {"start": v(184.5, 53.49) * mm, "end": v(216.62, 53.69) * mm});
            skLineSegment(sketch, "E910.MirrorCS", {"start": v(527.23, 54.07) * mm, "end": v(540.1, 54.15) * mm});
            skLineSegment(sketch, "E911.MirrorCS", {"start": v(184.5, 60.35) * mm, "end": v(216.63, 60.63) * mm});
            skLineSegment(sketch, "E912.MirrorCS", {"start": v(184.5, 36.7) * mm, "end": v(216.63, 36.75) * mm});
            skLineSegment(sketch, "E913.MirrorCS", {"start": v(527.22, 46.36) * mm, "end": v(540.1, 46.4) * mm});
            skLineSegment(sketch, "E914.MirrorCS", {"start": v(506.85, 53.94) * mm, "end": v(520.88, 54.03) * mm});
            skLineSegment(sketch, "E915.MirrorCS", {"start": v(259.28, 53.95) * mm, "end": v(287.2, 54.12) * mm});
            skLineSegment(sketch, "E916.MirrorCS", {"start": v(222.98, 45.24) * mm, "end": v(252.94, 45.35) * mm});
            skLineSegment(sketch, "E917.MirrorCS", {"start": v(325.91, 61.57) * mm, "end": v(350.1, 61.78) * mm});
            skLineSegment(sketch, "E918.MirrorCS", {"start": v(293.55, 62.82) * mm, "end": v(319.55, 63.04) * mm});
            skLineSegment(sketch, "E919.MirrorCS", {"start": v(385.27, 53.2) * mm, "end": v(406.12, 53.32) * mm});
            skLineSegment(sketch, "E920.MirrorCS", {"start": v(222.98, 52.2) * mm, "end": v(252.94, 52.38) * mm});
            skLineSegment(sketch, "E921.MirrorCS", {"start": v(485.25, 55.33) * mm, "end": v(500.49, 55.43) * mm});
            skLineSegment(sketch, "E922.MirrorCS", {"start": v(385.27, 45.84) * mm, "end": v(406.12, 45.91) * mm});
            skLineSegment(sketch, "E923.MirrorCS", {"start": v(6.35, 50.87) * mm, "end": v(48.47, 51.13) * mm});
            skLineSegment(sketch, "E924.MirrorCS", {"start": v(506.84, 55.47) * mm, "end": v(520.87, 55.55) * mm});
            skLineSegment(sketch, "E925.MirrorCS", {"start": v(462.38, 44.6) * mm, "end": v(478.9, 44.66) * mm});
            skLineSegment(sketch, "E926.MirrorCS", {"start": v(325.92, 44.1) * mm, "end": v(350.1, 44.18) * mm});
            skLineSegment(sketch, "E927.MirrorCS", {"start": v(412.46, 54.89) * mm, "end": v(431.79, 55) * mm});
            skLineSegment(sketch, "E928.MirrorCS", {"start": v(293.56, 45.5) * mm, "end": v(319.56, 45.6) * mm});
            skLineSegment(sketch, "E929.MirrorCS", {"start": v(506.85, 37.1) * mm, "end": v(520.88, 37.12) * mm});
            skLineSegment(sketch, "E930.MirrorCS", {"start": v(0, 59.53) * mm, "end": v(646.64, 65.09) * mm, "construction": true});
            skLineSegment(sketch, "E931.MirrorCS", {"start": v(6.36, 58.82) * mm, "end": v(48.48, 59.19) * mm});
            skLineSegment(sketch, "E932.MirrorCS", {"start": v(54.82, 59.24) * mm, "end": v(94.22, 59.58) * mm});
            skLineSegment(sketch, "E933.MirrorCS", {"start": v(143.75, 60) * mm, "end": v(178.15, 60.3) * mm});
            skLineSegment(sketch, "E934.MirrorCS", {"start": v(462.38, 46.12) * mm, "end": v(478.9, 46.18) * mm});
            skLineSegment(sketch, "E935.MirrorCS", {"start": v(259.3, 43.85) * mm, "end": v(287.22, 43.95) * mm});
            skLineSegment(sketch, "E936.MirrorCS", {"start": v(412.47, 44.41) * mm, "end": v(431.8, 44.48) * mm});
            skLineSegment(sketch, "E937.MirrorCS", {"start": v(143.74, 53.24) * mm, "end": v(178.14, 53.45) * mm});
            skLineSegment(sketch, "E938.MirrorCS", {"start": v(184.5, 51.96) * mm, "end": v(216.63, 52.16) * mm});
            skLineSegment(sketch, "E939.MirrorCS", {"start": v(325.9, 63.1) * mm, "end": v(350.08, 63.3) * mm});
            skLineSegment(sketch, "E940.MirrorCS", {"start": v(184.49, 61.88) * mm, "end": v(216.62, 62.15) * mm, "construction": true});
            skLineSegment(sketch, "E941.MirrorCS", {"start": v(143.75, 51.71) * mm, "end": v(178.15, 51.93) * mm});
            skLineSegment(sketch, "E942.MirrorCS", {"start": v(438.14, 46.03) * mm, "end": v(456.03, 46.1) * mm});
            skLineSegment(sketch, "E943.MirrorCS", {"start": v(259.29, 61) * mm, "end": v(287.21, 61.24) * mm});
            skLineSegment(sketch, "E944.MirrorCS", {"start": v(356.44, 54.54) * mm, "end": v(378.9, 54.68) * mm});
            skLineSegment(sketch, "E945.MirrorCS", {"start": v(293.57, 43.98) * mm, "end": v(319.57, 44.07) * mm});
            skLineSegment(sketch, "E946.MirrorCS", {"start": v(438.15, 44.5) * mm, "end": v(456.03, 44.57) * mm});
            skLineSegment(sketch, "E947.MirrorCS", {"start": v(184.5, 45.1) * mm, "end": v(216.63, 45.22) * mm});
            skLineSegment(sketch, "E948.MirrorCS", {"start": v(222.97, 62.2) * mm, "end": v(252.93, 62.47) * mm});
            skLineSegment(sketch, "E949.MirrorCS", {"start": v(527.23, 44.84) * mm, "end": v(540.11, 44.88) * mm});
            skLineSegment(sketch, "E950.MirrorCS", {"start": v(438.14, 55.04) * mm, "end": v(456.02, 55.15) * mm});
            skLineSegment(sketch, "E951.MirrorCS", {"start": v(100.57, 44.79) * mm, "end": v(137.4, 44.92) * mm});
            skLineSegment(sketch, "E952.MirrorCS", {"start": v(546.46, 44.9) * mm, "end": v(558.27, 44.95) * mm});
            skLineSegment(sketch, "E953.MirrorCS", {"start": v(6.35, 52.4) * mm, "end": v(48.46, 52.65) * mm});
            skLineSegment(sketch, "E954.MirrorCS", {"start": v(-33.04, 63.5) * mm, "end": v(118.54, 63.5) * mm, "construction": true});
            skLineSegment(sketch, "E955.MirrorCS", {"start": v(527.2, 64.82) * mm, "end": v(540.09, 64.93) * mm});
            skLineSegment(sketch, "E956.MirrorCS", {"start": v(293.56, 61.3) * mm, "end": v(319.56, 61.52) * mm});
            skLineSegment(sketch, "E957.MirrorCS", {"start": v(438.14, 62.53) * mm, "end": v(456.02, 62.69) * mm});
            skLineSegment(sketch, "E958.MirrorCS", {"start": v(54.82, 36.55) * mm, "end": v(94.22, 36.6) * mm});
            skLineSegment(sketch, "E959.MirrorCS", {"start": v(485.26, 35.55) * mm, "end": v(500.5, 35.57) * mm});
            skLineSegment(sketch, "E960.MirrorCS", {"start": v(325.91, 45.62) * mm, "end": v(350.1, 45.7) * mm});
            skLineSegment(sketch, "E961.MirrorCS", {"start": v(54.81, 52.7) * mm, "end": v(94.21, 52.93) * mm});
            skLineSegment(sketch, "E962.MirrorCS", {"start": v(54.82, 43.1) * mm, "end": v(94.22, 43.24) * mm});
            skLineSegment(sketch, "E963.MirrorCS", {"start": v(546.45, 55.7) * mm, "end": v(558.26, 55.78) * mm});
            skLineSegment(sketch, "E964.MirrorCS", {"start": v(485.26, 53.8) * mm, "end": v(500.5, 53.9) * mm});
            skLineSegment(sketch, "E965.MirrorCS", {"start": v(546.45, 63.46) * mm, "end": v(558.26, 63.57) * mm});
            skLineSegment(sketch, "E966.MirrorCS", {"start": v(6.35, 42.92) * mm, "end": v(48.47, 43.07) * mm});
            skLineSegment(sketch, "E967.MirrorCS", {"start": v(293.56, 54.16) * mm, "end": v(319.55, 54.32) * mm});
            skLineSegment(sketch, "E968.MirrorCS", {"start": v(325.91, 52.83) * mm, "end": v(350.1, 52.98) * mm});
            skLineSegment(sketch, "E969.MirrorCS", {"start": v(462.38, 53.67) * mm, "end": v(478.9, 53.77) * mm});
            skLineSegment(sketch, "E970.MirrorCS", {"start": v(527.22, 63.3) * mm, "end": v(540.1, 63.41) * mm});
            skLineSegment(sketch, "E971.MirrorCS", {"start": v(293.56, 36.84) * mm, "end": v(319.56, 36.87) * mm});
            skLineSegment(sketch, "E972.MirrorCS", {"start": v(506.84, 46.28) * mm, "end": v(520.87, 46.34) * mm});
            skLineSegment(sketch, "E973.MirrorCS", {"start": v(412.47, 45.94) * mm, "end": v(431.8, 46) * mm});
            skLineSegment(sketch, "E974.MirrorCS", {"start": v(385.26, 54.72) * mm, "end": v(406.11, 54.85) * mm});
            skLineSegment(sketch, "E975.MirrorCS", {"start": v(506.83, 64.65) * mm, "end": v(520.85, 64.77) * mm});
            skLineSegment(sketch, "E976.MirrorCS", {"start": v(385.27, 36.95) * mm, "end": v(406.12, 36.98) * mm});
            skLineSegment(sketch, "E977.MirrorCS", {"start": v(485.25, 46.2) * mm, "end": v(500.5, 46.26) * mm});
            skLineSegment(sketch, "E978.MirrorCS", {"start": v(222.98, 43.72) * mm, "end": v(252.94, 43.83) * mm});
            skLineSegment(sketch, "E979.MirrorCS", {"start": v(385.27, 44.31) * mm, "end": v(406.12, 44.39) * mm});
            skLineSegment(sketch, "E980.MirrorCS", {"start": v(100.57, 51.45) * mm, "end": v(137.4, 51.68) * mm});
            skLineSegment(sketch, "E981.MirrorCS", {"start": v(222.98, 60.69) * mm, "end": v(252.94, 60.94) * mm});
            skLineSegment(sketch, "E982.MirrorCS", {"start": v(527.22, 55.6) * mm, "end": v(540.1, 55.67) * mm});
            skLineSegment(sketch, "E983.MirrorCS", {"start": v(259.29, 45.37) * mm, "end": v(287.21, 45.48) * mm});
            skLineSegment(sketch, "E984.MirrorCS", {"start": v(506.85, 44.76) * mm, "end": v(520.88, 44.81) * mm});
            skLineSegment(sketch, "E985.MirrorCS", {"start": v(222.97, 53.72) * mm, "end": v(252.93, 53.9) * mm});
            skLineSegment(sketch, "E986.MirrorCS", {"start": v(259.28, 62.52) * mm, "end": v(287.2, 62.76) * mm});
            skLineSegment(sketch, "E987.MirrorCS", {"start": v(506.84, 63.12) * mm, "end": v(520.87, 63.24) * mm});
            skLineSegment(sketch, "E988.MirrorCS", {"start": v(0, 43.66) * mm, "end": v(646.66, 46.04) * mm, "construction": true});
            skLineSegment(sketch, "E989.MirrorCS", {"start": v(356.44, 45.73) * mm, "end": v(378.92, 45.81) * mm});
            skLineSegment(sketch, "E990.MirrorCS", {"start": v(100.57, 36.6) * mm, "end": v(137.4, 36.65) * mm});
            skLineSegment(sketch, "E991.MirrorCS", {"start": v(100.56, 52.97) * mm, "end": v(137.4, 53.2) * mm});
            skLineSegment(sketch, "E992.MirrorCS", {"start": v(356.43, 63.36) * mm, "end": v(378.9, 63.55) * mm});
            skLineSegment(sketch, "E993.MirrorCS", {"start": v(54.82, 35.02) * mm, "end": v(94.22, 35.07) * mm});
            skLineSegment(sketch, "E994.MirrorCS", {"start": v(462.38, 36.29) * mm, "end": v(462.38, 37.05) * mm});
            skLineSegment(sketch, "E995.MirrorCS", {"start": v(431.8, 37.01) * mm, "end": v(431.8, 36.25) * mm});
            skLineSegment(sketch, "E996.MirrorCS", {"start": v(143.74, 61.53) * mm, "end": v(178.14, 61.82) * mm});
            skLineSegment(sketch, "E997.MirrorCS", {"start": v(438.15, 36.26) * mm, "end": v(438.15, 37.02) * mm});
            skLineSegment(sketch, "E998.MirrorCS", {"start": v(356.45, 36.92) * mm, "end": v(378.92, 36.95) * mm});
            skLineSegment(sketch, "E999.MirrorCS", {"start": v(385.25, 63.6) * mm, "end": v(406.1, 63.78) * mm});
            skLineSegment(sketch, "E1000.MirrorCS", {"start": v(0, 50.83) * mm, "end": v(642.97, 54.78) * mm, "construction": true});
            skLineSegment(sketch, "E1001.MirrorCS", {"start": v(100.57, 43.26) * mm, "end": v(137.4, 43.4) * mm});
            skLineSegment(sketch, "E1002.MirrorCS", {"start": v(259.3, 36.8) * mm, "end": v(287.21, 36.83) * mm});
            skLineSegment(sketch, "E1003.MirrorCS", {"start": v(478.9, 37.07) * mm, "end": v(478.9, 36.3) * mm});
            skLineSegment(sketch, "E1004.MirrorCS", {"start": v(462.37, 62.74) * mm, "end": v(478.9, 62.88) * mm});
            skLineSegment(sketch, "E1005.MirrorCS", {"start": v(222.98, 35.23) * mm, "end": v(252.94, 35.27) * mm});
            skLineSegment(sketch, "E1006.MirrorCS", {"start": v(485.26, 37.08) * mm, "end": v(500.5, 37.1) * mm});
            skLineSegment(sketch, "E1007.MirrorCS", {"start": v(438.13, 64.06) * mm, "end": v(456.01, 64.21) * mm});
            skLineSegment(sketch, "E1008.MirrorCS", {"start": v(6.35, 34.96) * mm, "end": v(48.47, 35.02) * mm});
            skLineSegment(sketch, "E1009.MirrorCS", {"start": v(412.47, 36.99) * mm, "end": v(431.8, 37.01) * mm});
            skLineSegment(sketch, "E1010.MirrorCS", {"start": v(0, 58.77) * mm, "end": v(642.96, 64.3) * mm, "construction": true});
            skLineSegment(sketch, "E1011.MirrorCS", {"start": v(100.57, 59.63) * mm, "end": v(137.4, 59.95) * mm});
            skLineSegment(sketch, "E1012.MirrorCS", {"start": v(462.36, 64.27) * mm, "end": v(478.89, 64.4) * mm});
            skLineSegment(sketch, "E1013.MirrorCS", {"start": v(412.46, 62.31) * mm, "end": v(431.8, 62.48) * mm});
            skLineSegment(sketch, "E1014.MirrorCS", {"start": v(143.75, 36.66) * mm, "end": v(178.15, 36.7) * mm});
            skLineSegment(sketch, "E1015.MirrorCS", {"start": v(184.5, 35.18) * mm, "end": v(216.63, 35.22) * mm});
            skLineSegment(sketch, "E1016.MirrorCS", {"start": v(0, 51.6) * mm, "end": v(646.65, 55.56) * mm, "construction": true});
            skLineSegment(sketch, "E1017.MirrorCS", {"start": v(6.35, 36.49) * mm, "end": v(48.47, 36.54) * mm});
            skLineSegment(sketch, "E1018.MirrorCS", {"start": v(546.46, 37.15) * mm, "end": v(558.27, 37.17) * mm});
            skLineSegment(sketch, "E1019.MirrorCS", {"start": v(100.56, 61.16) * mm, "end": v(137.4, 61.47) * mm});
            skLineSegment(sketch, "E1020.MirrorCS", {"start": v(438.15, 37.02) * mm, "end": v(456.03, 37.04) * mm});
            skLineSegment(sketch, "E1021.MirrorCS", {"start": v(143.75, 35.13) * mm, "end": v(178.15, 35.18) * mm});
            skLineSegment(sketch, "E1022.MirrorCS", {"start": v(184.49, 61.88) * mm, "end": v(216.62, 62.15) * mm});
            skLineSegment(sketch, "E1023.MirrorCS", {"start": v(462.39, 35.52) * mm, "end": v(478.91, 35.54) * mm});
            skLineSegment(sketch, "E1024.MirrorCS", {"start": v(412.45, 63.84) * mm, "end": v(431.78, 64) * mm});
            skLineSegment(sketch, "E1025.MirrorCS", {"start": v(485.24, 64.46) * mm, "end": v(500.48, 64.6) * mm});
            skLineSegment(sketch, "E1026.MirrorCS", {"start": v(385.26, 62.08) * mm, "end": v(406.12, 62.26) * mm});
            skLineSegment(sketch, "E1027.MirrorCS", {"start": v(222.98, 36.75) * mm, "end": v(252.94, 36.8) * mm});
            skLineSegment(sketch, "E1028.MirrorCS", {"start": v(100.57, 35.08) * mm, "end": v(137.4, 35.13) * mm});
            skLineSegment(sketch, "E1029.MirrorCS", {"start": v(0, 42.9) * mm, "end": v(642.97, 45.26) * mm, "construction": true});
            skLineSegment(sketch, "E1030.MirrorCS", {"start": v(527.23, 37.13) * mm, "end": v(540.11, 37.14) * mm});
            skLineSegment(sketch, "E1031.MirrorCS", {"start": v(456.03, 37.04) * mm, "end": v(456.03, 36.28) * mm});
            skLineSegment(sketch, "E1032.MirrorCS", {"start": v(325.92, 35.36) * mm, "end": v(350.1, 35.39) * mm});
            skLineSegment(sketch, "E1033.MirrorCS", {"start": v(356.45, 35.4) * mm, "end": v(378.92, 35.42) * mm});
            skLineSegment(sketch, "E1034.MirrorCS", {"start": v(385.27, 36.2) * mm, "end": v(385.27, 35.43) * mm});
            skLineSegment(sketch, "E1035.MirrorCS", {"start": v(385.27, 35.43) * mm, "end": v(406.12, 35.46) * mm});
            skLineSegment(sketch, "E1036.MirrorCS", {"start": v(406.12, 35.46) * mm, "end": v(406.12, 36.22) * mm});
            skLineSegment(sketch, "E1037.MirrorCS", {"start": v(0, 34.96) * mm, "end": v(642.98, 35.75) * mm, "construction": true});
            skSolve(sketch);
        }
        {
            var Q0;
            Q0=qCreatedBy(makeId("Front.planeOp"),FACE);
            var sketch = newSketch(context, id + "F1", { "sketchPlane" : qUnion([Q0])});
            skLineSegment(sketch, "E1038", {"start": v(0, 0) * mm, "end": v(0, 63.5) * mm});
            skLineSegment(sketch, "E1039", {"start": v(0, 63.5) * mm, "end": v(635, 69.85) * mm});
            skLineSegment(sketch, "E1040", {"start": v(635, 69.85) * mm, "end": v(635, -6.35) * mm});
            skLineSegment(sketch, "E1041", {"start": v(635, -6.35) * mm, "end": v(0, 0) * mm});
            skLineSegment(sketch, "E1042", {"start": v(0, 31.75) * mm, "end": v(897.35, 31.75) * mm, "construction": true});
            skSolve(sketch);
        }
        {
            var Q0;
            Q0 = qSketchRegion(id + "F1", true);
            extrude(context, id + "F2", {"entities" : qUnion([Q0]), "depth" : 2.54 * mm});
        }
        {
            var Q0;
            Q0 = qSketchRegion(id + "F0", true);
            extrude(context, id + "F3", {"entities" : qUnion([Q0]), "operationType" : NewBodyOperationType.REMOVE, "endBound" : BoundingType.THROUGH_ALL, "depth" : 25.4 * mm});
        }
    });
